# Revit family: 1000_Sliding_Window_XO_Standard
name_source: partatom
category: Windows
revit_build: Autodesk Revit 2014 (Build: 20130308_1515(x64)
units: mm (PartAtom-declared; Revit-internal decimal feet)

## types (120) — shared parameters
Centered In Wall = Yes
Default Sill Height = 800 mm
Description = Sliding window, XO
Equal Sash Width = Yes
Frame Thickness = 76 mm
Limit Sash Height Max = 1800 mm  [stored 5.90551 ft]
Limit Sash Height Min = 300 mm
Limit Sash Width Max = 1500 mm  [stored 4.92126 ft]
Limit Sash Width Min = 300 mm
Limit Window Height Max = 1857 mm
Limit Window Height Min = 357 mm
Limit Window Width Max = 2999 mm
Limit Window Width Min = 599 mm
Manufacturer = Crealco
Model = 1000
Sash Frame Seal = 2 mm  [stored 0.00656168 ft]
URL = http://www.crealco.co.za
Wall Closure = By host
zero-valued in all types: Custom Frame Offset From Exterior, Custom Sash Width Left

## per-type parameters (varying)
- 1000SW-0906XO-1000Pa: Area Left Sash Glazing=0.15 m²; Area Right Sash Glazing=0.15 m²; Clearvue SHGC Value=0.521; Clearvue U Value=6.66; Custom Windload=1000 mm  [stored 3.28084 ft]; Custom Window Height=590 mm  [stored 1.9357 ft]; Custom Window Width=890 mm  [stored 2.91995 ft]; Energy Advantage SHGC Value=0.469; Energy Advantage U Value=5.64; Heavy Duty Interlocker=No; Height=590 mm  [stored 1.9357 ft]; Intruderprufe LowE SHGC Value=0.429; Intruderprufe LowE U Value=5.22; Intruderprufe SHGC Value=0.492; Intruderprufe U Value=6.2; Is Heavy Duty Mullion=0 mm  [stored 0 ft]; Limit Sash Width Left Max=591 mm; Limit Sash Width Left Min=300 mm; Max Pane Area=0.15 m²; Sash Height=533 mm; Sash Width Left=446 mm; Sash Width Right=446 mm; Standard Interlocker=Yes; Width=890 mm  [stored 2.91995 ft]; Windload Design=1000 mm  [stored 3.28084 ft]
- 1000SW-1206XO-1000Pa: Area Left Sash Glazing=0.21 m²; Area Right Sash Glazing=0.21 m²; Clearvue SHGC Value=0.546; Clearvue U Value=6.69; Custom Windload=1000 mm  [stored 3.28084 ft]; Custom Window Height=590 mm  [stored 1.9357 ft]; Custom Window Width=1190 mm  [stored 3.9042 ft]; Energy Advantage SHGC Value=0.491; Energy Advantage U Value=5.56; Heavy Duty Interlocker=No; Height=590 mm  [stored 1.9357 ft]; Intruderprufe LowE SHGC Value=0.449; Intruderprufe LowE U Value=5.14; Intruderprufe SHGC Value=0.515; Intruderprufe U Value=6.22; Is Heavy Duty Mullion=0 mm  [stored 0 ft]; Limit Sash Width Left Max=891 mm; Limit Sash Width Left Min=300 mm; Max Pane Area=0.21 m²; Sash Height=533 mm; Sash Width Left=596 mm; Sash Width Right=596 mm; Standard Interlocker=Yes; Width=1190 mm  [stored 3.9042 ft]; Windload Design=1000 mm  [stored 3.28084 ft]
- 1000SW-1506XO-1000Pa: Area Left Sash Glazing=0.28 m²; Area Right Sash Glazing=0.28 m²; Clearvue SHGC Value=0.562; Clearvue U Value=6.71; Custom Windload=1000 mm  [stored 3.28084 ft]; Custom Window Height=590 mm  [stored 1.9357 ft]; Custom Window Width=1490 mm  [stored 4.88845 ft]; Energy Advantage SHGC Value=0.505; Energy Advantage U Value=5.52; Heavy Duty Interlocker=No; Height=590 mm  [stored 1.9357 ft]; Intruderprufe LowE SHGC Value=0.461; Intruderprufe LowE U Value=5.08; Intruderprufe SHGC Value=0.529; Intruderprufe U Value=6.23; Is Heavy Duty Mullion=0 mm  [stored 0 ft]; Limit Sash Width Left Max=1191 mm; Limit Sash Width Left Min=300 mm; Max Pane Area=0.28 m²; Sash Height=533 mm; Sash Width Left=746 mm; Sash Width Right=746 mm; Standard Interlocker=Yes; Width=1490 mm  [stored 4.88845 ft]; Windload Design=1000 mm  [stored 3.28084 ft]
- 1000SW-1806XO-1000Pa: Area Left Sash Glazing=0.34 m²; Area Right Sash Glazing=0.34 m²; Clearvue SHGC Value=0.572; Clearvue U Value=6.73; Custom Windload=1000 mm  [stored 3.28084 ft]; Custom Window Height=590 mm  [stored 1.9357 ft]; Custom Window Width=1790 mm  [stored 5.8727 ft]; Energy Advantage SHGC Value=0.513; Energy Advantage U Value=5.49; Heavy Duty Interlocker=No; Height=590 mm  [stored 1.9357 ft]; Intruderprufe LowE SHGC Value=4.69; Intruderprufe LowE U Value=5.05; Intruderprufe SHGC Value=0.539; Intruderprufe U Value=6.24; Is Heavy Duty Mullion=0 mm  [stored 0 ft]; Limit Sash Width Left Max=1491 mm; Limit Sash Width Left Min=300 mm; Max Pane Area=0.34 m²; Sash Height=533 mm; Sash Width Left=896 mm; Sash Width Right=896 mm; Standard Interlocker=Yes; Width=1790 mm  [stored 5.8727 ft]; Windload Design=1000 mm  [stored 3.28084 ft]
- 1000SW-2106XO-1000Pa: Area Left Sash Glazing=0.41 m²; Area Right Sash Glazing=0.41 m²; Clearvue SHGC Value=0.579; Clearvue U Value=6.74; Custom Windload=1000 mm  [stored 3.28084 ft]; Custom Window Height=590 mm  [stored 1.9357 ft]; Custom Window Width=2090 mm  [stored 6.85696 ft]; Energy Advantage SHGC Value=0.52; Energy Advantage U Value=5.47; Heavy Duty Interlocker=No; Height=590 mm  [stored 1.9357 ft]; Intruderprufe LowE SHGC Value=0.474; Intruderprufe LowE U Value=5.02; Intruderprufe SHGC Value=0.545; Intruderprufe U Value=6.24; Is Heavy Duty Mullion=0 mm  [stored 0 ft]; Limit Sash Width Left Max=1500 mm  [stored 4.92126 ft]; Limit Sash Width Left Min=591 mm; Max Pane Area=0.41 m²; Sash Height=533 mm; Sash Width Left=1046 mm; Sash Width Right=1046 mm; Standard Interlocker=Yes; Width=2090 mm  [stored 6.85696 ft]; Windload Design=1000 mm  [stored 3.28084 ft]
- 1000SW-2406XO-1000Pa: Area Left Sash Glazing=0.47 m²; Area Right Sash Glazing=0.47 m²; Clearvue SHGC Value=0.584; Clearvue U Value=6.75; Custom Windload=1000 mm  [stored 3.28084 ft]; Custom Window Height=590 mm  [stored 1.9357 ft]; Custom Window Width=2390 mm  [stored 7.84121 ft]; Energy Advantage SHGC Value=0.524; Energy Advantage U Value=5.46; Heavy Duty Interlocker=No; Height=590 mm  [stored 1.9357 ft]; Intruderprufe LowE SHGC Value=0.479; Intruderprufe LowE U Value=5; Intruderprufe SHGC Value=0.55; Intruderprufe U Value=6.25; Is Heavy Duty Mullion=0 mm  [stored 0 ft]; Limit Sash Width Left Max=1500 mm  [stored 4.92126 ft]; Limit Sash Width Left Min=891 mm; Max Pane Area=0.47 m²; Sash Height=533 mm; Sash Width Left=1196 mm; Sash Width Right=1196 mm; Standard Interlocker=Yes; Width=2390 mm  [stored 7.84121 ft]; Windload Design=1000 mm  [stored 3.28084 ft]
- 1000SW-2706XO-1000Pa: Area Left Sash Glazing=0.54 m²; Area Right Sash Glazing=0.54 m²; Clearvue SHGC Value=0.588; Clearvue U Value=6.75; Custom Windload=1000 mm  [stored 3.28084 ft]; Custom Window Height=590 mm  [stored 1.9357 ft]; Custom Window Width=2690 mm; Energy Advantage SHGC Value=0.528; Energy Advantage U Value=5.44; Heavy Duty Interlocker=No; Height=590 mm  [stored 1.9357 ft]; Intruderprufe LowE SHGC Value=0.482; Intruderprufe LowE U Value=4.99; Intruderprufe SHGC Value=0.544; Intruderprufe U Value=6.25; Is Heavy Duty Mullion=0 mm  [stored 0 ft]; Limit Sash Width Left Max=1500 mm  [stored 4.92126 ft]; Limit Sash Width Left Min=1191 mm; Max Pane Area=0.54 m²; Sash Height=533 mm; Sash Width Left=1346 mm; Sash Width Right=1346 mm; Standard Interlocker=Yes; Width=2690 mm; Windload Design=1000 mm  [stored 3.28084 ft]
- 1000SW-3006XO-1000Pa: Area Left Sash Glazing=0.6 m²; Area Right Sash Glazing=0.6 m²; Clearvue SHGC Value=0.592; Clearvue U Value=6.76; Custom Windload=1000 mm  [stored 3.28084 ft]; Custom Window Height=590 mm  [stored 1.9357 ft]; Custom Window Width=2990 mm  [stored 9.80971 ft]; Energy Advantage SHGC Value=0.531; Energy Advantage U Value=5.43; Heavy Duty Interlocker=No; Height=590 mm  [stored 1.9357 ft]; Intruderprufe LowE SHGC Value=0.484; Intruderprufe LowE U Value=4.98; Intruderprufe SHGC Value=0.557; Intruderprufe U Value=6.25; Is Heavy Duty Mullion=0 mm  [stored 0 ft]; Limit Sash Width Left Max=1500 mm  [stored 4.92126 ft]; Limit Sash Width Left Min=1491 mm; Max Pane Area=0.6 m²; Sash Height=533 mm; Sash Width Left=1496 mm; Sash Width Right=1496 mm; Standard Interlocker=Yes; Width=2990 mm  [stored 9.80971 ft]; Windload Design=1000 mm  [stored 3.28084 ft]
- 1000SW-0909XO-1000Pa: Area Left Sash Glazing=0.25 m²; Area Right Sash Glazing=0.25 m²; Clearvue SHGC Value=0.585; Clearvue U Value=6.4; Custom Windload=1000 mm  [stored 3.28084 ft]; Custom Window Height=890 mm  [stored 2.91995 ft]; Custom Window Width=890 mm  [stored 2.91995 ft]; Energy Advantage SHGC Value=0.525; Energy Advantage U Value=5.21; Heavy Duty Interlocker=No; Height=890 mm  [stored 2.91995 ft]; Intruderprufe LowE SHGC Value=0.485; Intruderprufe LowE U Value=4.91; Intruderprufe SHGC Value=0.554; Intruderprufe U Value=6.05; Is Heavy Duty Mullion=0 mm  [stored 0 ft]; Limit Sash Width Left Max=591 mm; Limit Sash Width Left Min=300 mm; Max Pane Area=0.25 m²; Sash Height=833 mm; Sash Width Left=446 mm; Sash Width Right=446 mm; Standard Interlocker=Yes; Width=890 mm  [stored 2.91995 ft]; Windload Design=1000 mm  [stored 3.28084 ft]
- 1000SW-1209XO-1000Pa: Area Left Sash Glazing=0.36 m²; Area Right Sash Glazing=0.36 m²; Clearvue SHGC Value=0.614; Clearvue U Value=6.42; Custom Windload=1000 mm  [stored 3.28084 ft]; Custom Window Height=890 mm  [stored 2.91995 ft]; Custom Window Width=1190 mm  [stored 3.9042 ft]; Energy Advantage SHGC Value=0.55; Energy Advantage U Value=5.11; Heavy Duty Interlocker=No; Height=890 mm  [stored 2.91995 ft]; Intruderprufe LowE SHGC Value=0.507; Intruderprufe LowE U Value=4.8; Intruderprufe SHGC Value=0.58; Intruderprufe U Value=6.06; Is Heavy Duty Mullion=0 mm  [stored 0 ft]; Limit Sash Width Left Max=891 mm; Limit Sash Width Left Min=300 mm; Max Pane Area=0.36 m²; Sash Height=833 mm; Sash Width Left=596 mm; Sash Width Right=596 mm; Standard Interlocker=Yes; Width=1190 mm  [stored 3.9042 ft]; Windload Design=1000 mm  [stored 3.28084 ft]
- 1000SW-1509XO-1000Pa: Area Left Sash Glazing=0.47 m²; Area Right Sash Glazing=0.47 m²; Clearvue SHGC Value=0.631; Clearvue U Value=6.43; Custom Windload=1000 mm  [stored 3.28084 ft]; Custom Window Height=890 mm  [stored 2.91995 ft]; Custom Window Width=1490 mm  [stored 4.88845 ft]; Energy Advantage SHGC Value=0.565; Energy Advantage U Value=5.04; Heavy Duty Interlocker=No; Height=890 mm  [stored 2.91995 ft]; Intruderprufe LowE SHGC Value=0.521; Intruderprufe LowE U Value=4.73; Intruderprufe SHGC Value=0.596; Intruderprufe U Value=6.07; Is Heavy Duty Mullion=0 mm  [stored 0 ft]; Limit Sash Width Left Max=1191 mm; Limit Sash Width Left Min=300 mm; Max Pane Area=0.47 m²; Sash Height=833 mm; Sash Width Left=746 mm; Sash Width Right=746 mm; Standard Interlocker=Yes; Width=1490 mm  [stored 4.88845 ft]; Windload Design=1000 mm  [stored 3.28084 ft]
- 1000SW-1809XO-1000Pa: Area Left Sash Glazing=0.58 m²; Area Right Sash Glazing=0.58 m²; Clearvue SHGC Value=0.642; Clearvue U Value=6.44; Custom Windload=1000 mm  [stored 3.28084 ft]; Custom Window Height=890 mm  [stored 2.91995 ft]; Custom Window Width=1790 mm  [stored 5.8727 ft]; Energy Advantage SHGC Value=0.575; Energy Advantage U Value=5; Heavy Duty Interlocker=No; Height=890 mm  [stored 2.91995 ft]; Intruderprufe LowE SHGC Value=0.53; Intruderprufe LowE U Value=4.68; Intruderprufe SHGC Value=0.607; Intruderprufe U Value=6.08; Is Heavy Duty Mullion=0 mm  [stored 0 ft]; Limit Sash Width Left Max=1491 mm; Limit Sash Width Left Min=300 mm; Max Pane Area=0.58 m²; Sash Height=833 mm; Sash Width Left=896 mm; Sash Width Right=896 mm; Standard Interlocker=Yes; Width=1790 mm  [stored 5.8727 ft]; Windload Design=1000 mm  [stored 3.28084 ft]
- 1000SW-2109XO-1000Pa: Area Left Sash Glazing=0.69 m²; Area Right Sash Glazing=0.69 m²; Clearvue SHGC Value=0.65; Clearvue U Value=6.45; Custom Windload=1000 mm  [stored 3.28084 ft]; Custom Window Height=890 mm  [stored 2.91995 ft]; Custom Window Width=2090 mm  [stored 6.85696 ft]; Energy Advantage SHGC Value=0.583; Energy Advantage U Value=4.97; Heavy Duty Interlocker=No; Height=890 mm  [stored 2.91995 ft]; Intruderprufe LowE SHGC Value=0.536; Intruderprufe LowE U Value=4.65; Intruderprufe SHGC Value=0.614; Intruderprufe U Value=6.08; Is Heavy Duty Mullion=0 mm  [stored 0 ft]; Limit Sash Width Left Max=1500 mm  [stored 4.92126 ft]; Limit Sash Width Left Min=591 mm; Max Pane Area=0.69 m²; Sash Height=833 mm; Sash Width Left=1046 mm; Sash Width Right=1046 mm; Standard Interlocker=Yes; Width=2090 mm  [stored 6.85696 ft]; Windload Design=1000 mm  [stored 3.28084 ft]
- 1000SW-2409XO-1000Pa: Area Left Sash Glazing=0.8 m²; Area Right Sash Glazing=0.8 m²; Clearvue SHGC Value=0.656; Clearvue U Value=6.45; Custom Windload=1000 mm  [stored 3.28084 ft]; Custom Window Height=890 mm  [stored 2.91995 ft]; Custom Window Width=2390 mm  [stored 7.84121 ft]; Energy Advantage SHGC Value=0.588; Energy Advantage U Value=4.95; Heavy Duty Interlocker=No; Height=890 mm  [stored 2.91995 ft]; Intruderprufe LowE SHGC Value=0.541; Intruderprufe LowE U Value=4.62; Intruderprufe SHGC Value=0.62; Intruderprufe U Value=6.08; Is Heavy Duty Mullion=0 mm  [stored 0 ft]; Limit Sash Width Left Max=1500 mm  [stored 4.92126 ft]; Limit Sash Width Left Min=891 mm; Max Pane Area=0.8 m²; Sash Height=833 mm; Sash Width Left=1196 mm; Sash Width Right=1196 mm; Standard Interlocker=Yes; Width=2390 mm  [stored 7.84121 ft]; Windload Design=1000 mm  [stored 3.28084 ft]
- 1000SW-2709XO-1000Pa: Area Left Sash Glazing=0.91 m²; Area Right Sash Glazing=0.91 m²; Clearvue SHGC Value=0.661; Clearvue U Value=6.46; Custom Windload=1000 mm  [stored 3.28084 ft]; Custom Window Height=890 mm  [stored 2.91995 ft]; Custom Window Width=2690 mm; Energy Advantage SHGC Value=0.592; Energy Advantage U Value=4.93; Heavy Duty Interlocker=No; Height=890 mm  [stored 2.91995 ft]; Intruderprufe LowE SHGC Value=0.545; Intruderprufe LowE U Value=4.61; Intruderprufe SHGC Value=0.624; Intruderprufe U Value=6.08; Is Heavy Duty Mullion=0 mm  [stored 0 ft]; Limit Sash Width Left Max=1500 mm  [stored 4.92126 ft]; Limit Sash Width Left Min=1191 mm; Max Pane Area=0.91 m²; Sash Height=833 mm; Sash Width Left=1346 mm; Sash Width Right=1346 mm; Standard Interlocker=Yes; Width=2690 mm; Windload Design=1000 mm  [stored 3.28084 ft]
- 1000SW-3009XO-1000Pa: Area Left Sash Glazing=1.02 m²; Area Right Sash Glazing=1.02 m²; Clearvue SHGC Value=0.665; Clearvue U Value=6.46; Custom Windload=1000 mm  [stored 3.28084 ft]; Custom Window Height=890 mm  [stored 2.91995 ft]; Custom Window Width=2990 mm  [stored 9.80971 ft]; Energy Advantage SHGC Value=0.595; Energy Advantage U Value=4.92; Heavy Duty Interlocker=No; Height=890 mm  [stored 2.91995 ft]; Intruderprufe LowE SHGC Value=0.548; Intruderprufe LowE U Value=4.59; Intruderprufe SHGC Value=0.628; Intruderprufe U Value=6.08; Is Heavy Duty Mullion=0 mm  [stored 0 ft]; Limit Sash Width Left Max=1500 mm  [stored 4.92126 ft]; Limit Sash Width Left Min=1491 mm; Max Pane Area=1.02 m²; Sash Height=833 mm; Sash Width Left=1496 mm; Sash Width Right=1496 mm; Standard Interlocker=Yes; Width=2990 mm  [stored 9.80971 ft]; Windload Design=1000 mm  [stored 3.28084 ft]
- 1000SW-0912XO-1000Pa: Area Left Sash Glazing=0.36 m²; Area Right Sash Glazing=0.36 m²; Clearvue SHGC Value=0.616; Clearvue U Value=6.27; Custom Windload=1000 mm  [stored 3.28084 ft]; Custom Window Height=1190 mm  [stored 3.9042 ft]; Custom Window Width=890 mm  [stored 2.91995 ft]; Energy Advantage SHGC Value=0.553; Energy Advantage U Value=5; Heavy Duty Interlocker=No; Height=1190 mm  [stored 3.9042 ft]; Intruderprufe LowE SHGC Value=0.512; Intruderprufe LowE U Value=4.76; Intruderprufe SHGC Value=0.584; Intruderprufe U Value=5.98; Is Heavy Duty Mullion=0 mm  [stored 0 ft]; Limit Sash Width Left Max=591 mm; Limit Sash Width Left Min=300 mm; Max Pane Area=0.36 m²; Sash Height=1133 mm; Sash Width Left=446 mm; Sash Width Right=446 mm; Standard Interlocker=Yes; Width=890 mm  [stored 2.91995 ft]; Windload Design=1000 mm  [stored 3.28084 ft]
- 1000SW-1212XO-1000Pa: Area Left Sash Glazing=0.51 m²; Area Right Sash Glazing=0.51 m²; Clearvue SHGC Value=0.647; Clearvue U Value=6.29; Custom Windload=1000 mm  [stored 3.28084 ft]; Custom Window Height=1190 mm  [stored 3.9042 ft]; Custom Window Width=1190 mm  [stored 3.9042 ft]; Energy Advantage SHGC Value=0.58; Energy Advantage U Value=4.88; Heavy Duty Interlocker=No; Height=1190 mm  [stored 3.9042 ft]; Intruderprufe LowE SHGC Value=0.536; Intruderprufe LowE U Value=4.63; Intruderprufe SHGC Value=0.613; Intruderprufe U Value=5.99; Is Heavy Duty Mullion=0 mm  [stored 0 ft]; Limit Sash Width Left Max=891 mm; Limit Sash Width Left Min=300 mm; Max Pane Area=0.51 m²; Sash Height=1133 mm; Sash Width Left=596 mm; Sash Width Right=596 mm; Standard Interlocker=Yes; Width=1190 mm  [stored 3.9042 ft]; Windload Design=1000 mm  [stored 3.28084 ft]
- 1000SW-1512XO-1000Pa: Area Left Sash Glazing=0.67 m²; Area Right Sash Glazing=0.67 m²; Clearvue SHGC Value=0.665; Clearvue U Value=6.3; Custom Windload=1000 mm  [stored 3.28084 ft]; Custom Window Height=1190 mm  [stored 3.9042 ft]; Custom Window Width=1490 mm  [stored 4.88845 ft]; Energy Advantage SHGC Value=0.596; Energy Advantage U Value=4.81; Heavy Duty Interlocker=No; Height=1190 mm  [stored 3.9042 ft]; Intruderprufe LowE SHGC Value=0.55; Intruderprufe LowE U Value=4; Intruderprufe SHGC Value=0.629; Intruderprufe U Value=5.99; Is Heavy Duty Mullion=0 mm  [stored 0 ft]; Limit Sash Width Left Max=1191 mm; Limit Sash Width Left Min=300 mm; Max Pane Area=0.67 m²; Sash Height=1133 mm; Sash Width Left=746 mm; Sash Width Right=746 mm; Standard Interlocker=Yes; Width=1490 mm  [stored 4.88845 ft]; Windload Design=1000 mm  [stored 3.28084 ft]
- 1000SW-1812XO-1000Pa: Area Left Sash Glazing=0.82 m²; Area Right Sash Glazing=0.82 m²; Clearvue SHGC Value=0.677; Clearvue U Value=6.3; Custom Windload=1000 mm  [stored 3.28084 ft]; Custom Window Height=1190 mm  [stored 3.9042 ft]; Custom Window Width=1790 mm  [stored 5.8727 ft]; Energy Advantage SHGC Value=0.606; Energy Advantage U Value=4.76; Heavy Duty Interlocker=No; Height=1190 mm  [stored 3.9042 ft]; Intruderprufe LowE SHGC Value=0.56; Intruderprufe LowE U Value=4.5; Intruderprufe SHGC Value=0.641; Intruderprufe U Value=5.99; Is Heavy Duty Mullion=0 mm  [stored 0 ft]; Limit Sash Width Left Max=1491 mm; Limit Sash Width Left Min=300 mm; Max Pane Area=0.82 m²; Sash Height=1133 mm; Sash Width Left=896 mm; Sash Width Right=896 mm; Standard Interlocker=Yes; Width=1790 mm  [stored 5.8727 ft]; Windload Design=1000 mm  [stored 3.28084 ft]
- 1000SW-2112XO-1000Pa: Area Left Sash Glazing=0.98 m²; Area Right Sash Glazing=0.98 m²; Clearvue SHGC Value=0.686; Clearvue U Value=6.31; Custom Windload=1000 mm  [stored 3.28084 ft]; Custom Window Height=1190 mm  [stored 3.9042 ft]; Custom Window Width=2090 mm  [stored 6.85696 ft]; Energy Advantage SHGC Value=0.614; Energy Advantage U Value=4.72; Heavy Duty Interlocker=No; Height=1190 mm  [stored 3.9042 ft]; Intruderprufe LowE SHGC Value=0.567; Intruderprufe LowE U Value=4.46; Intruderprufe SHGC Value=0.649; Intruderprufe U Value=6; Is Heavy Duty Mullion=0 mm  [stored 0 ft]; Limit Sash Width Left Max=1500 mm  [stored 4.92126 ft]; Limit Sash Width Left Min=591 mm; Max Pane Area=0.98 m²; Sash Height=1133 mm; Sash Width Left=1046 mm; Sash Width Right=1046 mm; Standard Interlocker=Yes; Width=2090 mm  [stored 6.85696 ft]; Windload Design=1000 mm  [stored 3.28084 ft]
- 1000SW-2412XO-1000Pa: Area Left Sash Glazing=1.13 m²; Area Right Sash Glazing=1.13 m²; Clearvue SHGC Value=0.692; Clearvue U Value=6.31; Custom Windload=1000 mm  [stored 3.28084 ft]; Custom Window Height=1190 mm  [stored 3.9042 ft]; Custom Window Width=2390 mm  [stored 7.84121 ft]; Energy Advantage SHGC Value=0.619; Energy Advantage U Value=4.7; Heavy Duty Interlocker=No; Height=1190 mm  [stored 3.9042 ft]; Intruderprufe LowE SHGC Value=0.572; Intruderprufe LowE U Value=4.44; Intruderprufe SHGC Value=0.655; Intruderprufe U Value=6; Is Heavy Duty Mullion=0 mm  [stored 0 ft]; Limit Sash Width Left Max=1500 mm  [stored 4.92126 ft]; Limit Sash Width Left Min=891 mm; Max Pane Area=1.13 m²; Sash Height=1133 mm; Sash Width Left=1196 mm; Sash Width Right=1196 mm; Standard Interlocker=Yes; Width=2390 mm  [stored 7.84121 ft]; Windload Design=1000 mm  [stored 3.28084 ft]
- 1000SW-2712XO-1000Pa: Area Left Sash Glazing=1.28 m²; Area Right Sash Glazing=1.28 m²; Clearvue SHGC Value=0.679; Clearvue U Value=6.31; Custom Windload=1000 mm  [stored 3.28084 ft]; Custom Window Height=1190 mm  [stored 3.9042 ft]; Custom Window Width=2690 mm; Energy Advantage SHGC Value=0.624; Energy Advantage U Value=4.68; Heavy Duty Interlocker=No; Height=1190 mm  [stored 3.9042 ft]; Intruderprufe LowE SHGC Value=0.576; Intruderprufe LowE U Value=4.42; Intruderprufe SHGC Value=0.659; Intruderprufe U Value=6; Is Heavy Duty Mullion=0 mm  [stored 0 ft]; Limit Sash Width Left Max=1500 mm  [stored 4.92126 ft]; Limit Sash Width Left Min=1191 mm; Max Pane Area=1.28 m²; Sash Height=1133 mm; Sash Width Left=1346 mm; Sash Width Right=1346 mm; Standard Interlocker=Yes; Width=2690 mm; Windload Design=1000 mm  [stored 3.28084 ft]
- 1000SW-3012XO-1000Pa: Area Left Sash Glazing=1.44 m²; Area Right Sash Glazing=1.44 m²; Clearvue SHGC Value=0.701; Clearvue U Value=6.31; Custom Windload=1000 mm  [stored 3.28084 ft]; Custom Window Height=1190 mm  [stored 3.9042 ft]; Custom Window Width=2990 mm  [stored 9.80971 ft]; Energy Advantage SHGC Value=0.627; Energy Advantage U Value=4.66; Heavy Duty Interlocker=No; Height=1190 mm  [stored 3.9042 ft]; Intruderprufe LowE SHGC Value=0.579; Intruderprufe LowE U Value=4.4; Intruderprufe SHGC Value=0.663; Intruderprufe U Value=6; Is Heavy Duty Mullion=0 mm  [stored 0 ft]; Limit Sash Width Left Max=1500 mm  [stored 4.92126 ft]; Limit Sash Width Left Min=1491 mm; Max Pane Area=1.44 m²; Sash Height=1133 mm; Sash Width Left=1496 mm; Sash Width Right=1496 mm; Standard Interlocker=Yes; Width=2990 mm  [stored 9.80971 ft]; Windload Design=1000 mm  [stored 3.28084 ft]
- 1000SW-0915XO-1000Pa: Area Left Sash Glazing=0.46 m²; Area Right Sash Glazing=0.46 m²; Clearvue SHGC Value=0.635; Clearvue U Value=6.19; Custom Windload=1000 mm  [stored 3.28084 ft]; Custom Window Height=1490 mm  [stored 4.88845 ft]; Custom Window Width=890 mm  [stored 2.91995 ft]; Energy Advantage SHGC Value=0.57; Energy Advantage U Value=4.87; Heavy Duty Interlocker=No; Height=1490 mm  [stored 4.88845 ft]; Intruderprufe LowE SHGC Value=0.528; Intruderprufe LowE U Value=4.67; Intruderprufe SHGC Value=0.603; Intruderprufe U Value=5.94; Is Heavy Duty Mullion=0 mm  [stored 0 ft]; Limit Sash Width Left Max=591 mm; Limit Sash Width Left Min=300 mm; Max Pane Area=0.46 m²; Sash Height=1433 mm; Sash Width Left=446 mm; Sash Width Right=446 mm; Standard Interlocker=Yes; Width=890 mm  [stored 2.91995 ft]; Windload Design=1000 mm  [stored 3.28084 ft]
- 1000SW-1215XO-1000Pa: Area Left Sash Glazing=0.66 m²; Area Right Sash Glazing=0.66 m²; Clearvue SHGC Value=0.667; Clearvue U Value=6.2; Custom Windload=1000 mm  [stored 3.28084 ft]; Custom Window Height=1490 mm  [stored 4.88845 ft]; Custom Window Width=1190 mm  [stored 3.9042 ft]; Energy Advantage SHGC Value=0.597; Energy Advantage U Value=4.74; Heavy Duty Interlocker=No; Height=1490 mm  [stored 4.88845 ft]; Intruderprufe LowE SHGC Value=0.553; Intruderprufe LowE U Value=4.53; Intruderprufe SHGC Value=0.632; Intruderprufe U Value=5.94; Is Heavy Duty Mullion=0 mm  [stored 0 ft]; Limit Sash Width Left Max=891 mm; Limit Sash Width Left Min=300 mm; Max Pane Area=0.66 m²; Sash Height=1433 mm; Sash Width Left=596 mm; Sash Width Right=596 mm; Standard Interlocker=Yes; Width=1190 mm  [stored 3.9042 ft]; Windload Design=1000 mm  [stored 3.28084 ft]
- 1000SW-1515XO-1000Pa: Area Left Sash Glazing=0.86 m²; Area Right Sash Glazing=0.86 m²; Clearvue SHGC Value=0.685; Clearvue U Value=6.21; Custom Windload=1000 mm  [stored 3.28084 ft]; Custom Window Height=1490 mm  [stored 4.88845 ft]; Custom Window Width=1490 mm  [stored 4.88845 ft]; Energy Advantage SHGC Value=0.614; Energy Advantage U Value=4.66; Heavy Duty Interlocker=No; Height=1490 mm  [stored 4.88845 ft]; Intruderprufe LowE SHGC Value=0.568; Intruderprufe LowE U Value=4.45; Intruderprufe SHGC Value=0.649; Intruderprufe U Value=5.94; Is Heavy Duty Mullion=0 mm  [stored 0 ft]; Limit Sash Width Left Max=1191 mm; Limit Sash Width Left Min=300 mm; Max Pane Area=0.86 m²; Sash Height=1433 mm; Sash Width Left=746 mm; Sash Width Right=746 mm; Standard Interlocker=Yes; Width=1490 mm  [stored 4.88845 ft]; Windload Design=1000 mm  [stored 3.28084 ft]
- 1000SW-1815XO-1000Pa: Area Left Sash Glazing=1.06 m²; Area Right Sash Glazing=1.06 m²; Clearvue SHGC Value=0.693; Clearvue U Value=6.22; Custom Windload=1000 mm  [stored 3.28084 ft]; Custom Window Height=1490 mm  [stored 4.88845 ft]; Custom Window Width=1790 mm  [stored 5.8727 ft]; Energy Advantage SHGC Value=0.625; Energy Advantage U Value=4.61; Heavy Duty Interlocker=No; Height=1490 mm  [stored 4.88845 ft]; Intruderprufe LowE SHGC Value=0.578; Intruderprufe LowE U Value=4.39; Intruderprufe SHGC Value=0.661; Intruderprufe U Value=5.95; Is Heavy Duty Mullion=0 mm  [stored 0 ft]; Limit Sash Width Left Max=1491 mm; Limit Sash Width Left Min=300 mm; Max Pane Area=1.06 m²; Sash Height=1433 mm; Sash Width Left=896 mm; Sash Width Right=896 mm; Standard Interlocker=Yes; Width=1790 mm  [stored 5.8727 ft]; Windload Design=1000 mm  [stored 3.28084 ft]
- 1000SW-2115XO-1000Pa: Area Left Sash Glazing=1.26 m²; Area Right Sash Glazing=1.26 m²; Clearvue SHGC Value=0.707; Clearvue U Value=6.22; Custom Windload=1000 mm  [stored 3.28084 ft]; Custom Window Height=1490 mm  [stored 4.88845 ft]; Custom Window Width=2090 mm  [stored 6.85696 ft]; Energy Advantage SHGC Value=0.632; Energy Advantage U Value=6.32; Heavy Duty Interlocker=No; Height=1490 mm  [stored 4.88845 ft]; Intruderprufe LowE SHGC Value=0.585; Intruderprufe LowE U Value=4.35; Intruderprufe SHGC Value=0.669; Intruderprufe U Value=5.95; Is Heavy Duty Mullion=0 mm  [stored 0 ft]; Limit Sash Width Left Max=1500 mm  [stored 4.92126 ft]; Limit Sash Width Left Min=591 mm; Max Pane Area=1.26 m²; Sash Height=1433 mm; Sash Width Left=1046 mm; Sash Width Right=1046 mm; Standard Interlocker=Yes; Width=2090 mm  [stored 6.85696 ft]; Windload Design=1000 mm  [stored 3.28084 ft]
- 1000SW-2415XO-1000Pa: Area Left Sash Glazing=1.46 m²; Area Right Sash Glazing=1.46 m²; Clearvue SHGC Value=0.713; Clearvue U Value=6.22; Custom Windload=1000 mm  [stored 3.28084 ft]; Custom Window Height=1490 mm  [stored 4.88845 ft]; Custom Window Width=2390 mm  [stored 7.84121 ft]; Energy Advantage SHGC Value=0.638; Energy Advantage U Value=4.55; Heavy Duty Interlocker=No; Height=1490 mm  [stored 4.88845 ft]; Intruderprufe LowE SHGC Value=0.59; Intruderprufe LowE U Value=4.33; Intruderprufe SHGC Value=0.675; Intruderprufe U Value=5.95; Is Heavy Duty Mullion=0 mm  [stored 0 ft]; Limit Sash Width Left Max=1500 mm  [stored 4.92126 ft]; Limit Sash Width Left Min=891 mm; Max Pane Area=1.46 m²; Sash Height=1433 mm; Sash Width Left=1196 mm; Sash Width Right=1196 mm; Standard Interlocker=Yes; Width=2390 mm  [stored 7.84121 ft]; Windload Design=1000 mm  [stored 3.28084 ft]
- 1000SW-2715XO-1000Pa: Area Left Sash Glazing=1.66 m²; Area Right Sash Glazing=1.66 m²; Clearvue SHGC Value=0.719; Clearvue U Value=6.23; Custom Windload=1000 mm  [stored 3.28084 ft]; Custom Window Height=1490 mm  [stored 4.88845 ft]; Custom Window Width=2690 mm; Energy Advantage SHGC Value=0.643; Energy Advantage U Value=4.53; Heavy Duty Interlocker=No; Height=1490 mm  [stored 4.88845 ft]; Intruderprufe LowE SHGC Value=0.594; Intruderprufe LowE U Value=4.3; Intruderprufe SHGC Value=0.68; Intruderprufe U Value=5.95; Is Heavy Duty Mullion=0 mm  [stored 0 ft]; Limit Sash Width Left Max=1500 mm  [stored 4.92126 ft]; Limit Sash Width Left Min=1191 mm; Max Pane Area=1.66 m²; Sash Height=1433 mm; Sash Width Left=1346 mm; Sash Width Right=1346 mm; Standard Interlocker=Yes; Width=2690 mm; Windload Design=1000 mm  [stored 3.28084 ft]
- 1000SW-3015XO-1000Pa: Area Left Sash Glazing=1.86 m²; Area Right Sash Glazing=1.86 m²; Clearvue SHGC Value=0.723; Clearvue U Value=6.23; Custom Windload=1000 mm  [stored 3.28084 ft]; Custom Window Height=1490 mm  [stored 4.88845 ft]; Custom Window Width=2990 mm  [stored 9.80971 ft]; Energy Advantage SHGC Value=0.646; Energy Advantage U Value=4.51; Heavy Duty Interlocker=No; Height=1490 mm  [stored 4.88845 ft]; Intruderprufe LowE SHGC Value=0.598; Intruderprufe LowE U Value=4.28; Intruderprufe SHGC Value=0.684; Intruderprufe U Value=5.95; Is Heavy Duty Mullion=0 mm  [stored 0 ft]; Limit Sash Width Left Max=1500 mm  [stored 4.92126 ft]; Limit Sash Width Left Min=1491 mm; Max Pane Area=1.86 m²; Sash Height=1433 mm; Sash Width Left=1496 mm; Sash Width Right=1496 mm; Standard Interlocker=Yes; Width=2990 mm  [stored 9.80971 ft]; Windload Design=1000 mm  [stored 3.28084 ft]
- 1000SW-1518XO-1000Pa: Area Left Sash Glazing=1.05 m²; Area Right Sash Glazing=1.05 m²; Clearvue SHGC Value=0.699; Clearvue U Value=6.16; Custom Windload=1000 mm  [stored 3.28084 ft]; Custom Window Height=1790 mm  [stored 5.8727 ft]; Custom Window Width=1490 mm  [stored 4.88845 ft]; Energy Advantage SHGC Value=0.626; Energy Advantage U Value=4.57; Heavy Duty Interlocker=Yes; Height=1790 mm  [stored 5.8727 ft]; Intruderprufe LowE SHGC Value=0.58; Intruderprufe LowE U Value=4.38; Intruderprufe SHGC Value=0.662; Intruderprufe U Value=5.91; Is Heavy Duty Mullion=1 mm  [stored 0.00328084 ft]; Limit Sash Width Left Max=1191 mm; Limit Sash Width Left Min=300 mm; Max Pane Area=1.05 m²; Sash Height=1733 mm; Sash Width Left=746 mm; Sash Width Right=746 mm; Standard Interlocker=No; Width=1490 mm  [stored 4.88845 ft]; Windload Design=1000 mm  [stored 3.28084 ft]
- 1000SW-1818XO-1000Pa: Area Left Sash Glazing=1.3 m²; Area Right Sash Glazing=1.3 m²; Clearvue SHGC Value=0.712; Clearvue U Value=6.16; Custom Windload=1000 mm  [stored 3.28084 ft]; Custom Window Height=1790 mm  [stored 5.8727 ft]; Custom Window Width=1790 mm  [stored 5.8727 ft]; Energy Advantage SHGC Value=0.637; Energy Advantage U Value=4.52; Heavy Duty Interlocker=Yes; Height=1790 mm  [stored 5.8727 ft]; Intruderprufe LowE SHGC Value=0.59; Intruderprufe LowE U Value=4.32; Intruderprufe SHGC Value=0.674; Intruderprufe U Value=5.91; Is Heavy Duty Mullion=1 mm  [stored 0.00328084 ft]; Limit Sash Width Left Max=1491 mm; Limit Sash Width Left Min=300 mm; Max Pane Area=1.3 m²; Sash Height=1733 mm; Sash Width Left=896 mm; Sash Width Right=896 mm; Standard Interlocker=No; Width=1790 mm  [stored 5.8727 ft]; Windload Design=1000 mm  [stored 3.28084 ft]
- 1000SW-2118XO-1000Pa: Area Left Sash Glazing=1.54 m²; Area Right Sash Glazing=1.54 m²; Clearvue SHGC Value=0.721; Clearvue U Value=6.16; Custom Windload=1000 mm  [stored 3.28084 ft]; Custom Window Height=1790 mm  [stored 5.8727 ft]; Custom Window Width=2090 mm  [stored 6.85696 ft]; Energy Advantage SHGC Value=0.645; Energy Advantage U Value=4.48; Heavy Duty Interlocker=Yes; Height=1790 mm  [stored 5.8727 ft]; Intruderprufe LowE SHGC Value=0.597; Intruderprufe LowE U Value=4.28; Intruderprufe SHGC Value=0.683; Intruderprufe U Value=5.92; Is Heavy Duty Mullion=1 mm  [stored 0.00328084 ft]; Limit Sash Width Left Max=1500 mm  [stored 4.92126 ft]; Limit Sash Width Left Min=591 mm; Max Pane Area=1.54 m²; Sash Height=1733 mm; Sash Width Left=1046 mm; Sash Width Right=1046 mm; Standard Interlocker=No; Width=2090 mm  [stored 6.85696 ft]; Windload Design=1000 mm  [stored 3.28084 ft]
- 1000SW-2418XO-1000Pa: Area Left Sash Glazing=1.79 m²; Area Right Sash Glazing=1.79 m²; Clearvue SHGC Value=0.728; Clearvue U Value=6.17; Custom Windload=1000 mm  [stored 3.28084 ft]; Custom Window Height=1790 mm  [stored 5.8727 ft]; Custom Window Width=2390 mm  [stored 7.84121 ft]; Energy Advantage SHGC Value=0.651; Energy Advantage U Value=4.45; Heavy Duty Interlocker=Yes; Height=1790 mm  [stored 5.8727 ft]; Intruderprufe LowE SHGC Value=0.425; Intruderprufe LowE U Value=4.28; Intruderprufe SHGC Value=0.689; Intruderprufe U Value=5.95; Is Heavy Duty Mullion=1 mm  [stored 0.00328084 ft]; Limit Sash Width Left Max=1500 mm  [stored 4.92126 ft]; Limit Sash Width Left Min=891 mm; Max Pane Area=1.79 m²; Sash Height=1733 mm; Sash Width Left=1196 mm; Sash Width Right=1196 mm; Standard Interlocker=No; Width=2390 mm  [stored 7.84121 ft]; Windload Design=1000 mm  [stored 3.28084 ft]
- 1000SW-2718XO-1000Pa: Area Left Sash Glazing=2.03 m²; Area Right Sash Glazing=2.03 m²; Clearvue SHGC Value=0.733; Clearvue U Value=6.17; Custom Windload=1000 mm  [stored 3.28084 ft]; Custom Window Height=1790 mm  [stored 5.8727 ft]; Custom Window Width=2690 mm; Energy Advantage SHGC Value=0.655; Energy Advantage U Value=4.43; Heavy Duty Interlocker=Yes; Height=1790 mm  [stored 5.8727 ft]; Intruderprufe LowE SHGC Value=0.607; Intruderprufe LowE U Value=4.23; Intruderprufe SHGC Value=0.694; Intruderprufe U Value=5.92; Is Heavy Duty Mullion=1 mm  [stored 0.00328084 ft]; Limit Sash Width Left Max=1500 mm  [stored 4.92126 ft]; Limit Sash Width Left Min=1191 mm; Max Pane Area=2.03 m²; Sash Height=1733 mm; Sash Width Left=1346 mm; Sash Width Right=1346 mm; Standard Interlocker=No; Width=2690 mm; Windload Design=1000 mm  [stored 3.28084 ft]
- 1000SW-3018XO-1000Pa: Area Left Sash Glazing=2.28 m²; Area Right Sash Glazing=2.28 m²; Clearvue SHGC Value=0.737; Clearvue U Value=6.17; Custom Windload=1000 mm  [stored 3.28084 ft]; Custom Window Height=1790 mm  [stored 5.8727 ft]; Custom Window Width=2990 mm  [stored 9.80971 ft]; Energy Advantage SHGC Value=0.659; Energy Advantage U Value=4.41; Heavy Duty Interlocker=Yes; Height=1790 mm  [stored 5.8727 ft]; Intruderprufe LowE SHGC Value=0.61; Intruderprufe LowE U Value=4.21; Intruderprufe SHGC Value=0.698; Intruderprufe U Value=5.92; Is Heavy Duty Mullion=1 mm  [stored 0.00328084 ft]; Limit Sash Width Left Max=1500 mm  [stored 4.92126 ft]; Limit Sash Width Left Min=1491 mm; Max Pane Area=2.28 m²; Sash Height=1733 mm; Sash Width Left=1496 mm; Sash Width Right=1496 mm; Standard Interlocker=No; Width=2990 mm  [stored 9.80971 ft]; Windload Design=1000 mm  [stored 3.28084 ft]
- 1000SW-0918XO-1000Pa: Area Left Sash Glazing=0.56 m²; Area Right Sash Glazing=0.56 m²; Clearvue SHGC Value=0.648; Clearvue U Value=6.14; Custom Windload=1000 mm  [stored 3.28084 ft]; Custom Window Height=1790 mm  [stored 5.8727 ft]; Custom Window Width=890 mm  [stored 2.91995 ft]; Energy Advantage SHGC Value=0.581; Energy Advantage U Value=4.79; Heavy Duty Interlocker=No; Height=1790 mm  [stored 5.8727 ft]; Intruderprufe LowE SHGC Value=0.539; Intruderprufe LowE U Value=4.61; Intruderprufe SHGC Value=0.615; Intruderprufe U Value=5.91; Is Heavy Duty Mullion=0 mm  [stored 0 ft]; Limit Sash Width Left Max=591 mm; Limit Sash Width Left Min=300 mm; Max Pane Area=0.56 m²; Sash Height=1733 mm; Sash Width Left=446 mm; Sash Width Right=446 mm; Standard Interlocker=Yes; Width=890 mm  [stored 2.91995 ft]; Windload Design=1000 mm  [stored 3.28084 ft]
- 1000SW-1218XO-1000Pa: Area Left Sash Glazing=0.81 m²; Area Right Sash Glazing=0.81 m²; Clearvue SHGC Value=0.68; Clearvue U Value=6.15; Custom Windload=1000 mm  [stored 3.28084 ft]; Custom Window Height=1790 mm  [stored 5.8727 ft]; Custom Window Width=1190 mm  [stored 3.9042 ft]; Energy Advantage SHGC Value=0.609; Energy Advantage U Value=4.65; Heavy Duty Interlocker=No; Height=1790 mm  [stored 5.8727 ft]; Intruderprufe LowE SHGC Value=0.565; Intruderprufe LowE U Value=4.46; Intruderprufe SHGC Value=0.645; Intruderprufe U Value=5.91; Is Heavy Duty Mullion=0 mm  [stored 0 ft]; Limit Sash Width Left Max=891 mm; Limit Sash Width Left Min=300 mm; Max Pane Area=0.81 m²; Sash Height=1733 mm; Sash Width Left=596 mm; Sash Width Right=596 mm; Standard Interlocker=Yes; Width=1190 mm  [stored 3.9042 ft]; Windload Design=1000 mm  [stored 3.28084 ft]
- 1000SW-0906XO-1500Pa: Area Left Sash Glazing=0.15 m²; Area Right Sash Glazing=0.15 m²; Clearvue SHGC Value=0.521; Clearvue U Value=6.66; Custom Windload=1500 mm  [stored 4.92126 ft]; Custom Window Height=590 mm  [stored 1.9357 ft]; Custom Window Width=890 mm  [stored 2.91995 ft]; Energy Advantage SHGC Value=0.469; Energy Advantage U Value=5.64; Heavy Duty Interlocker=No; Height=590 mm  [stored 1.9357 ft]; Intruderprufe LowE SHGC Value=0.429; Intruderprufe LowE U Value=5.22; Intruderprufe SHGC Value=0.492; Intruderprufe U Value=6.2; Is Heavy Duty Mullion=0 mm  [stored 0 ft]; Limit Sash Width Left Max=591 mm; Limit Sash Width Left Min=300 mm; Max Pane Area=0.15 m²; Sash Height=533 mm; Sash Width Left=446 mm; Sash Width Right=446 mm; Standard Interlocker=Yes; Width=890 mm  [stored 2.91995 ft]; Windload Design=1500 mm  [stored 4.92126 ft]
- 1000SW-0906XO-2000Pa: Area Left Sash Glazing=0.15 m²; Area Right Sash Glazing=0.15 m²; Clearvue SHGC Value=0.521; Clearvue U Value=6.66; Custom Windload=2000 mm  [stored 6.56168 ft]; Custom Window Height=590 mm  [stored 1.9357 ft]; Custom Window Width=890 mm  [stored 2.91995 ft]; Energy Advantage SHGC Value=0.469; Energy Advantage U Value=5.64; Heavy Duty Interlocker=No; Height=590 mm  [stored 1.9357 ft]; Intruderprufe LowE SHGC Value=0.429; Intruderprufe LowE U Value=5.22; Intruderprufe SHGC Value=0.492; Intruderprufe U Value=6.2; Is Heavy Duty Mullion=0 mm  [stored 0 ft]; Limit Sash Width Left Max=591 mm; Limit Sash Width Left Min=300 mm; Max Pane Area=0.15 m²; Sash Height=533 mm; Sash Width Left=446 mm; Sash Width Right=446 mm; Standard Interlocker=Yes; Width=890 mm  [stored 2.91995 ft]; Windload Design=2000 mm  [stored 6.56168 ft]
- 1000SW-0909XO-1500Pa: Area Left Sash Glazing=0.25 m²; Area Right Sash Glazing=0.25 m²; Clearvue SHGC Value=0.585; Clearvue U Value=6.4; Custom Windload=1500 mm  [stored 4.92126 ft]; Custom Window Height=890 mm  [stored 2.91995 ft]; Custom Window Width=890 mm  [stored 2.91995 ft]; Energy Advantage SHGC Value=0.525; Energy Advantage U Value=5.21; Heavy Duty Interlocker=No; Height=890 mm  [stored 2.91995 ft]; Intruderprufe LowE SHGC Value=0.485; Intruderprufe LowE U Value=4.91; Intruderprufe SHGC Value=0.554; Intruderprufe U Value=6.05; Is Heavy Duty Mullion=0 mm  [stored 0 ft]; Limit Sash Width Left Max=591 mm; Limit Sash Width Left Min=300 mm; Max Pane Area=0.25 m²; Sash Height=833 mm; Sash Width Left=446 mm; Sash Width Right=446 mm; Standard Interlocker=Yes; Width=890 mm  [stored 2.91995 ft]; Windload Design=1500 mm  [stored 4.92126 ft]
- 1000SW-0909XO-2000Pa: Area Left Sash Glazing=0.25 m²; Area Right Sash Glazing=0.25 m²; Clearvue SHGC Value=0.585; Clearvue U Value=6.4; Custom Windload=2000 mm  [stored 6.56168 ft]; Custom Window Height=890 mm  [stored 2.91995 ft]; Custom Window Width=890 mm  [stored 2.91995 ft]; Energy Advantage SHGC Value=0.525; Energy Advantage U Value=5.21; Heavy Duty Interlocker=No; Height=890 mm  [stored 2.91995 ft]; Intruderprufe LowE SHGC Value=0.485; Intruderprufe LowE U Value=4.91; Intruderprufe SHGC Value=0.554; Intruderprufe U Value=6.05; Is Heavy Duty Mullion=0 mm  [stored 0 ft]; Limit Sash Width Left Max=591 mm; Limit Sash Width Left Min=300 mm; Max Pane Area=0.25 m²; Sash Height=833 mm; Sash Width Left=446 mm; Sash Width Right=446 mm; Standard Interlocker=Yes; Width=890 mm  [stored 2.91995 ft]; Windload Design=2000 mm  [stored 6.56168 ft]
- 1000SW-0912XO-1500Pa: Area Left Sash Glazing=0.36 m²; Area Right Sash Glazing=0.36 m²; Clearvue SHGC Value=0.616; Clearvue U Value=6.27; Custom Windload=1500 mm  [stored 4.92126 ft]; Custom Window Height=1190 mm  [stored 3.9042 ft]; Custom Window Width=890 mm  [stored 2.91995 ft]; Energy Advantage SHGC Value=0.553; Energy Advantage U Value=5; Heavy Duty Interlocker=No; Height=1190 mm  [stored 3.9042 ft]; Intruderprufe LowE SHGC Value=0.512; Intruderprufe LowE U Value=4.76; Intruderprufe SHGC Value=0.584; Intruderprufe U Value=5.98; Is Heavy Duty Mullion=0 mm  [stored 0 ft]; Limit Sash Width Left Max=591 mm; Limit Sash Width Left Min=300 mm; Max Pane Area=0.36 m²; Sash Height=1133 mm; Sash Width Left=446 mm; Sash Width Right=446 mm; Standard Interlocker=Yes; Width=890 mm  [stored 2.91995 ft]; Windload Design=1500 mm  [stored 4.92126 ft]
- 1000SW-0912XO-2000Pa: Area Left Sash Glazing=0.36 m²; Area Right Sash Glazing=0.36 m²; Clearvue SHGC Value=0.616; Clearvue U Value=6.27; Custom Windload=2000 mm  [stored 6.56168 ft]; Custom Window Height=1190 mm  [stored 3.9042 ft]; Custom Window Width=890 mm  [stored 2.91995 ft]; Energy Advantage SHGC Value=0.553; Energy Advantage U Value=5; Heavy Duty Interlocker=No; Height=1190 mm  [stored 3.9042 ft]; Intruderprufe LowE SHGC Value=0.512; Intruderprufe LowE U Value=4.76; Intruderprufe SHGC Value=0.584; Intruderprufe U Value=5.98; Is Heavy Duty Mullion=0 mm  [stored 0 ft]; Limit Sash Width Left Max=591 mm; Limit Sash Width Left Min=300 mm; Max Pane Area=0.36 m²; Sash Height=1133 mm; Sash Width Left=446 mm; Sash Width Right=446 mm; Standard Interlocker=Yes; Width=890 mm  [stored 2.91995 ft]; Windload Design=2000 mm  [stored 6.56168 ft]
- 1000SW-0915XO-1500Pa: Area Left Sash Glazing=0.46 m²; Area Right Sash Glazing=0.46 m²; Clearvue SHGC Value=0.635; Clearvue U Value=6.19; Custom Windload=1500 mm  [stored 4.92126 ft]; Custom Window Height=1490 mm  [stored 4.88845 ft]; Custom Window Width=890 mm  [stored 2.91995 ft]; Energy Advantage SHGC Value=0.57; Energy Advantage U Value=4.87; Heavy Duty Interlocker=No; Height=1490 mm  [stored 4.88845 ft]; Intruderprufe LowE SHGC Value=0.528; Intruderprufe LowE U Value=4.67; Intruderprufe SHGC Value=0.603; Intruderprufe U Value=5.94; Is Heavy Duty Mullion=0 mm  [stored 0 ft]; Limit Sash Width Left Max=591 mm; Limit Sash Width Left Min=300 mm; Max Pane Area=0.46 m²; Sash Height=1433 mm; Sash Width Left=446 mm; Sash Width Right=446 mm; Standard Interlocker=Yes; Width=890 mm  [stored 2.91995 ft]; Windload Design=1500 mm  [stored 4.92126 ft]
- 1000SW-0915XO-2000Pa: Area Left Sash Glazing=0.46 m²; Area Right Sash Glazing=0.46 m²; Clearvue SHGC Value=0.635; Clearvue U Value=6.19; Custom Windload=2000 mm  [stored 6.56168 ft]; Custom Window Height=1490 mm  [stored 4.88845 ft]; Custom Window Width=890 mm  [stored 2.91995 ft]; Energy Advantage SHGC Value=0.57; Energy Advantage U Value=4.87; Heavy Duty Interlocker=No; Height=1490 mm  [stored 4.88845 ft]; Intruderprufe LowE SHGC Value=0.528; Intruderprufe LowE U Value=4.67; Intruderprufe SHGC Value=0.603; Intruderprufe U Value=5.94; Is Heavy Duty Mullion=0 mm  [stored 0 ft]; Limit Sash Width Left Max=591 mm; Limit Sash Width Left Min=300 mm; Max Pane Area=0.46 m²; Sash Height=1433 mm; Sash Width Left=446 mm; Sash Width Right=446 mm; Standard Interlocker=Yes; Width=890 mm  [stored 2.91995 ft]; Windload Design=2000 mm  [stored 6.56168 ft]
- 1000SW-0918XO-1500Pa: Area Left Sash Glazing=0.56 m²; Area Right Sash Glazing=0.56 m²; Clearvue SHGC Value=0.648; Clearvue U Value=6.14; Custom Windload=1500 mm  [stored 4.92126 ft]; Custom Window Height=1790 mm  [stored 5.8727 ft]; Custom Window Width=890 mm  [stored 2.91995 ft]; Energy Advantage SHGC Value=0.581; Energy Advantage U Value=4.79; Heavy Duty Interlocker=Yes; Height=1790 mm  [stored 5.8727 ft]; Intruderprufe LowE SHGC Value=0.539; Intruderprufe LowE U Value=4.61; Intruderprufe SHGC Value=0.615; Intruderprufe U Value=5.91; Is Heavy Duty Mullion=1 mm  [stored 0.00328084 ft]; Limit Sash Width Left Max=591 mm; Limit Sash Width Left Min=300 mm; Max Pane Area=0.56 m²; Sash Height=1733 mm; Sash Width Left=446 mm; Sash Width Right=446 mm; Standard Interlocker=No; Width=890 mm  [stored 2.91995 ft]; Windload Design=1500 mm  [stored 4.92126 ft]
- 1000SW-0918XO-2000Pa: Area Left Sash Glazing=0.56 m²; Area Right Sash Glazing=0.56 m²; Clearvue SHGC Value=0.648; Clearvue U Value=6.14; Custom Windload=2000 mm  [stored 6.56168 ft]; Custom Window Height=1790 mm  [stored 5.8727 ft]; Custom Window Width=890 mm  [stored 2.91995 ft]; Energy Advantage SHGC Value=0.581; Energy Advantage U Value=4.79; Heavy Duty Interlocker=Yes; Height=1790 mm  [stored 5.8727 ft]; Intruderprufe LowE SHGC Value=0.539; Intruderprufe LowE U Value=4.61; Intruderprufe SHGC Value=0.615; Intruderprufe U Value=5.91; Is Heavy Duty Mullion=1 mm  [stored 0.00328084 ft]; Limit Sash Width Left Max=591 mm; Limit Sash Width Left Min=300 mm; Max Pane Area=0.56 m²; Sash Height=1733 mm; Sash Width Left=446 mm; Sash Width Right=446 mm; Standard Interlocker=No; Width=890 mm  [stored 2.91995 ft]; Windload Design=2000 mm  [stored 6.56168 ft]
- 1000SW-1206XO-1500Pa: Area Left Sash Glazing=0.21 m²; Area Right Sash Glazing=0.21 m²; Clearvue SHGC Value=0.546; Clearvue U Value=6.69; Custom Windload=1500 mm  [stored 4.92126 ft]; Custom Window Height=590 mm  [stored 1.9357 ft]; Custom Window Width=1190 mm  [stored 3.9042 ft]; Energy Advantage SHGC Value=0.491; Energy Advantage U Value=5.56; Heavy Duty Interlocker=No; Height=590 mm  [stored 1.9357 ft]; Intruderprufe LowE SHGC Value=0.449; Intruderprufe LowE U Value=5.14; Intruderprufe SHGC Value=0.515; Intruderprufe U Value=6.22; Is Heavy Duty Mullion=0 mm  [stored 0 ft]; Limit Sash Width Left Max=891 mm; Limit Sash Width Left Min=300 mm; Max Pane Area=0.21 m²; Sash Height=533 mm; Sash Width Left=596 mm; Sash Width Right=596 mm; Standard Interlocker=Yes; Width=1190 mm  [stored 3.9042 ft]; Windload Design=1500 mm  [stored 4.92126 ft]
- 1000SW-1206XO-2000Pa: Area Left Sash Glazing=0.21 m²; Area Right Sash Glazing=0.21 m²; Clearvue SHGC Value=0.546; Clearvue U Value=6.69; Custom Windload=2000 mm  [stored 6.56168 ft]; Custom Window Height=590 mm  [stored 1.9357 ft]; Custom Window Width=1190 mm  [stored 3.9042 ft]; Energy Advantage SHGC Value=0.491; Energy Advantage U Value=5.56; Heavy Duty Interlocker=No; Height=590 mm  [stored 1.9357 ft]; Intruderprufe LowE SHGC Value=0.449; Intruderprufe LowE U Value=5.14; Intruderprufe SHGC Value=0.515; Intruderprufe U Value=6.22; Is Heavy Duty Mullion=0 mm  [stored 0 ft]; Limit Sash Width Left Max=891 mm; Limit Sash Width Left Min=300 mm; Max Pane Area=0.21 m²; Sash Height=533 mm; Sash Width Left=596 mm; Sash Width Right=596 mm; Standard Interlocker=Yes; Width=1190 mm  [stored 3.9042 ft]; Windload Design=2000 mm  [stored 6.56168 ft]
- 1000SW-1209XO-1500Pa: Area Left Sash Glazing=0.36 m²; Area Right Sash Glazing=0.36 m²; Clearvue SHGC Value=0.614; Clearvue U Value=6.42; Custom Windload=1500 mm  [stored 4.92126 ft]; Custom Window Height=890 mm  [stored 2.91995 ft]; Custom Window Width=1190 mm  [stored 3.9042 ft]; Energy Advantage SHGC Value=0.55; Energy Advantage U Value=5.11; Heavy Duty Interlocker=No; Height=890 mm  [stored 2.91995 ft]; Intruderprufe LowE SHGC Value=0.507; Intruderprufe LowE U Value=4.8; Intruderprufe SHGC Value=0.58; Intruderprufe U Value=6.06; Is Heavy Duty Mullion=0 mm  [stored 0 ft]; Limit Sash Width Left Max=891 mm; Limit Sash Width Left Min=300 mm; Max Pane Area=0.36 m²; Sash Height=833 mm; Sash Width Left=596 mm; Sash Width Right=596 mm; Standard Interlocker=Yes; Width=1190 mm  [stored 3.9042 ft]; Windload Design=1500 mm  [stored 4.92126 ft]
- 1000SW-1209XO-2000Pa: Area Left Sash Glazing=0.36 m²; Area Right Sash Glazing=0.36 m²; Clearvue SHGC Value=0.614; Clearvue U Value=6.42; Custom Windload=2000 mm  [stored 6.56168 ft]; Custom Window Height=890 mm  [stored 2.91995 ft]; Custom Window Width=1190 mm  [stored 3.9042 ft]; Energy Advantage SHGC Value=0.55; Energy Advantage U Value=5.11; Heavy Duty Interlocker=No; Height=890 mm  [stored 2.91995 ft]; Intruderprufe LowE SHGC Value=0.507; Intruderprufe LowE U Value=4.8; Intruderprufe SHGC Value=0.58; Intruderprufe U Value=6.06; Is Heavy Duty Mullion=0 mm  [stored 0 ft]; Limit Sash Width Left Max=891 mm; Limit Sash Width Left Min=300 mm; Max Pane Area=0.36 m²; Sash Height=833 mm; Sash Width Left=596 mm; Sash Width Right=596 mm; Standard Interlocker=Yes; Width=1190 mm  [stored 3.9042 ft]; Windload Design=2000 mm  [stored 6.56168 ft]
- 1000SW-1212XO-1500Pa: Area Left Sash Glazing=0.51 m²; Area Right Sash Glazing=0.51 m²; Clearvue SHGC Value=0.647; Clearvue U Value=6.29; Custom Windload=1500 mm  [stored 4.92126 ft]; Custom Window Height=1190 mm  [stored 3.9042 ft]; Custom Window Width=1190 mm  [stored 3.9042 ft]; Energy Advantage SHGC Value=0.58; Energy Advantage U Value=4.88; Heavy Duty Interlocker=No; Height=1190 mm  [stored 3.9042 ft]; Intruderprufe LowE SHGC Value=0.536; Intruderprufe LowE U Value=4.63; Intruderprufe SHGC Value=0.613; Intruderprufe U Value=5.99; Is Heavy Duty Mullion=0 mm  [stored 0 ft]; Limit Sash Width Left Max=891 mm; Limit Sash Width Left Min=300 mm; Max Pane Area=0.51 m²; Sash Height=1133 mm; Sash Width Left=596 mm; Sash Width Right=596 mm; Standard Interlocker=Yes; Width=1190 mm  [stored 3.9042 ft]; Windload Design=1500 mm  [stored 4.92126 ft]
- 1000SW-1212XO-2000Pa: Area Left Sash Glazing=0.51 m²; Area Right Sash Glazing=0.51 m²; Clearvue SHGC Value=0.647; Clearvue U Value=6.29; Custom Windload=2000 mm  [stored 6.56168 ft]; Custom Window Height=1190 mm  [stored 3.9042 ft]; Custom Window Width=1190 mm  [stored 3.9042 ft]; Energy Advantage SHGC Value=0.58; Energy Advantage U Value=4.88; Heavy Duty Interlocker=No; Height=1190 mm  [stored 3.9042 ft]; Intruderprufe LowE SHGC Value=0.536; Intruderprufe LowE U Value=4.63; Intruderprufe SHGC Value=0.613; Intruderprufe U Value=5.99; Is Heavy Duty Mullion=0 mm  [stored 0 ft]; Limit Sash Width Left Max=891 mm; Limit Sash Width Left Min=300 mm; Max Pane Area=0.51 m²; Sash Height=1133 mm; Sash Width Left=596 mm; Sash Width Right=596 mm; Standard Interlocker=Yes; Width=1190 mm  [stored 3.9042 ft]; Windload Design=2000 mm  [stored 6.56168 ft]
- 1000SW-1215XO-1500Pa: Area Left Sash Glazing=0.66 m²; Area Right Sash Glazing=0.66 m²; Clearvue SHGC Value=0.667; Clearvue U Value=6.2; Custom Windload=1500 mm  [stored 4.92126 ft]; Custom Window Height=1490 mm  [stored 4.88845 ft]; Custom Window Width=1190 mm  [stored 3.9042 ft]; Energy Advantage SHGC Value=0.597; Energy Advantage U Value=4.74; Heavy Duty Interlocker=No; Height=1490 mm  [stored 4.88845 ft]; Intruderprufe LowE SHGC Value=0.553; Intruderprufe LowE U Value=4.53; Intruderprufe SHGC Value=0.632; Intruderprufe U Value=5.94; Is Heavy Duty Mullion=0 mm  [stored 0 ft]; Limit Sash Width Left Max=891 mm; Limit Sash Width Left Min=300 mm; Max Pane Area=0.66 m²; Sash Height=1433 mm; Sash Width Left=596 mm; Sash Width Right=596 mm; Standard Interlocker=Yes; Width=1190 mm  [stored 3.9042 ft]; Windload Design=1500 mm  [stored 4.92126 ft]
- 1000SW-1215XO-2000Pa: Area Left Sash Glazing=0.66 m²; Area Right Sash Glazing=0.66 m²; Clearvue SHGC Value=0.667; Clearvue U Value=6.2; Custom Windload=2000 mm  [stored 6.56168 ft]; Custom Window Height=1490 mm  [stored 4.88845 ft]; Custom Window Width=1190 mm  [stored 3.9042 ft]; Energy Advantage SHGC Value=0.597; Energy Advantage U Value=4.74; Heavy Duty Interlocker=No; Height=1490 mm  [stored 4.88845 ft]; Intruderprufe LowE SHGC Value=0.553; Intruderprufe LowE U Value=4.53; Intruderprufe SHGC Value=0.632; Intruderprufe U Value=5.94; Is Heavy Duty Mullion=0 mm  [stored 0 ft]; Limit Sash Width Left Max=891 mm; Limit Sash Width Left Min=300 mm; Max Pane Area=0.66 m²; Sash Height=1433 mm; Sash Width Left=596 mm; Sash Width Right=596 mm; Standard Interlocker=Yes; Width=1190 mm  [stored 3.9042 ft]; Windload Design=2000 mm  [stored 6.56168 ft]
- 1000SW-1218XO-1500Pa: Area Left Sash Glazing=0.81 m²; Area Right Sash Glazing=0.81 m²; Clearvue SHGC Value=0.68; Clearvue U Value=6.15; Custom Windload=1500 mm  [stored 4.92126 ft]; Custom Window Height=1790 mm  [stored 5.8727 ft]; Custom Window Width=1190 mm  [stored 3.9042 ft]; Energy Advantage SHGC Value=0.609; Energy Advantage U Value=4.65; Heavy Duty Interlocker=Yes; Height=1790 mm  [stored 5.8727 ft]; Intruderprufe LowE SHGC Value=0.565; Intruderprufe LowE U Value=4.46; Intruderprufe SHGC Value=0.645; Intruderprufe U Value=5.91; Is Heavy Duty Mullion=1 mm  [stored 0.00328084 ft]; Limit Sash Width Left Max=891 mm; Limit Sash Width Left Min=300 mm; Max Pane Area=0.81 m²; Sash Height=1733 mm; Sash Width Left=596 mm; Sash Width Right=596 mm; Standard Interlocker=No; Width=1190 mm  [stored 3.9042 ft]; Windload Design=1500 mm  [stored 4.92126 ft]
- 1000SW-1218XO-2000Pa: Area Left Sash Glazing=0.81 m²; Area Right Sash Glazing=0.81 m²; Clearvue SHGC Value=0.68; Clearvue U Value=6.15; Custom Windload=2000 mm  [stored 6.56168 ft]; Custom Window Height=1790 mm  [stored 5.8727 ft]; Custom Window Width=1190 mm  [stored 3.9042 ft]; Energy Advantage SHGC Value=0.609; Energy Advantage U Value=4.65; Heavy Duty Interlocker=Yes; Height=1790 mm  [stored 5.8727 ft]; Intruderprufe LowE SHGC Value=0.565; Intruderprufe LowE U Value=4.46; Intruderprufe SHGC Value=0.645; Intruderprufe U Value=5.91; Is Heavy Duty Mullion=1 mm  [stored 0.00328084 ft]; Limit Sash Width Left Max=891 mm; Limit Sash Width Left Min=300 mm; Max Pane Area=0.81 m²; Sash Height=1733 mm; Sash Width Left=596 mm; Sash Width Right=596 mm; Standard Interlocker=No; Width=1190 mm  [stored 3.9042 ft]; Windload Design=2000 mm  [stored 6.56168 ft]
- 1000SW-1506XO-1500Pa: Area Left Sash Glazing=0.28 m²; Area Right Sash Glazing=0.28 m²; Clearvue SHGC Value=0.562; Clearvue U Value=6.71; Custom Windload=1500 mm  [stored 4.92126 ft]; Custom Window Height=590 mm  [stored 1.9357 ft]; Custom Window Width=1490 mm  [stored 4.88845 ft]; Energy Advantage SHGC Value=0.505; Energy Advantage U Value=5.52; Heavy Duty Interlocker=No; Height=590 mm  [stored 1.9357 ft]; Intruderprufe LowE SHGC Value=0.461; Intruderprufe LowE U Value=5.08; Intruderprufe SHGC Value=0.529; Intruderprufe U Value=6.23; Is Heavy Duty Mullion=0 mm  [stored 0 ft]; Limit Sash Width Left Max=1191 mm; Limit Sash Width Left Min=300 mm; Max Pane Area=0.28 m²; Sash Height=533 mm; Sash Width Left=746 mm; Sash Width Right=746 mm; Standard Interlocker=Yes; Width=1490 mm  [stored 4.88845 ft]; Windload Design=1500 mm  [stored 4.92126 ft]
- 1000SW-1506XO-2000Pa: Area Left Sash Glazing=0.28 m²; Area Right Sash Glazing=0.28 m²; Clearvue SHGC Value=0.562; Clearvue U Value=6.71; Custom Windload=2000 mm  [stored 6.56168 ft]; Custom Window Height=590 mm  [stored 1.9357 ft]; Custom Window Width=1490 mm  [stored 4.88845 ft]; Energy Advantage SHGC Value=0.505; Energy Advantage U Value=5.52; Heavy Duty Interlocker=No; Height=590 mm  [stored 1.9357 ft]; Intruderprufe LowE SHGC Value=0.461; Intruderprufe LowE U Value=5.08; Intruderprufe SHGC Value=0.529; Intruderprufe U Value=6.23; Is Heavy Duty Mullion=0 mm  [stored 0 ft]; Limit Sash Width Left Max=1191 mm; Limit Sash Width Left Min=300 mm; Max Pane Area=0.28 m²; Sash Height=533 mm; Sash Width Left=746 mm; Sash Width Right=746 mm; Standard Interlocker=Yes; Width=1490 mm  [stored 4.88845 ft]; Windload Design=2000 mm  [stored 6.56168 ft]
- 1000SW-1509XO-1500Pa: Area Left Sash Glazing=0.47 m²; Area Right Sash Glazing=0.47 m²; Clearvue SHGC Value=0.631; Clearvue U Value=6.43; Custom Windload=1500 mm  [stored 4.92126 ft]; Custom Window Height=890 mm  [stored 2.91995 ft]; Custom Window Width=1490 mm  [stored 4.88845 ft]; Energy Advantage SHGC Value=0.565; Energy Advantage U Value=5.04; Heavy Duty Interlocker=No; Height=890 mm  [stored 2.91995 ft]; Intruderprufe LowE SHGC Value=0.521; Intruderprufe LowE U Value=4.73; Intruderprufe SHGC Value=0.596; Intruderprufe U Value=6.07; Is Heavy Duty Mullion=0 mm  [stored 0 ft]; Limit Sash Width Left Max=1191 mm; Limit Sash Width Left Min=300 mm; Max Pane Area=0.47 m²; Sash Height=833 mm; Sash Width Left=746 mm; Sash Width Right=746 mm; Standard Interlocker=Yes; Width=1490 mm  [stored 4.88845 ft]; Windload Design=1500 mm  [stored 4.92126 ft]
- 1000SW-1509XO-2000Pa: Area Left Sash Glazing=0.47 m²; Area Right Sash Glazing=0.47 m²; Clearvue SHGC Value=0.631; Clearvue U Value=6.43; Custom Windload=2000 mm  [stored 6.56168 ft]; Custom Window Height=890 mm  [stored 2.91995 ft]; Custom Window Width=1490 mm  [stored 4.88845 ft]; Energy Advantage SHGC Value=0.565; Energy Advantage U Value=5.04; Heavy Duty Interlocker=No; Height=890 mm  [stored 2.91995 ft]; Intruderprufe LowE SHGC Value=0.521; Intruderprufe LowE U Value=4.73; Intruderprufe SHGC Value=0.596; Intruderprufe U Value=6.07; Is Heavy Duty Mullion=0 mm  [stored 0 ft]; Limit Sash Width Left Max=1191 mm; Limit Sash Width Left Min=300 mm; Max Pane Area=0.47 m²; Sash Height=833 mm; Sash Width Left=746 mm; Sash Width Right=746 mm; Standard Interlocker=Yes; Width=1490 mm  [stored 4.88845 ft]; Windload Design=2000 mm  [stored 6.56168 ft]
- 1000SW-1512XO-1500Pa: Area Left Sash Glazing=0.67 m²; Area Right Sash Glazing=0.67 m²; Clearvue SHGC Value=0.665; Clearvue U Value=6.3; Custom Windload=1500 mm  [stored 4.92126 ft]; Custom Window Height=1190 mm  [stored 3.9042 ft]; Custom Window Width=1490 mm  [stored 4.88845 ft]; Energy Advantage SHGC Value=0.596; Energy Advantage U Value=4.81; Heavy Duty Interlocker=No; Height=1190 mm  [stored 3.9042 ft]; Intruderprufe LowE SHGC Value=0.55; Intruderprufe LowE U Value=4; Intruderprufe SHGC Value=0.629; Intruderprufe U Value=5.99; Is Heavy Duty Mullion=0 mm  [stored 0 ft]; Limit Sash Width Left Max=1191 mm; Limit Sash Width Left Min=300 mm; Max Pane Area=0.67 m²; Sash Height=1133 mm; Sash Width Left=746 mm; Sash Width Right=746 mm; Standard Interlocker=Yes; Width=1490 mm  [stored 4.88845 ft]; Windload Design=1500 mm  [stored 4.92126 ft]
- 1000SW-1512XO-2000Pa: Area Left Sash Glazing=0.67 m²; Area Right Sash Glazing=0.67 m²; Clearvue SHGC Value=0.665; Clearvue U Value=6.3; Custom Windload=2000 mm  [stored 6.56168 ft]; Custom Window Height=1190 mm  [stored 3.9042 ft]; Custom Window Width=1490 mm  [stored 4.88845 ft]; Energy Advantage SHGC Value=0.596; Energy Advantage U Value=4.81; Heavy Duty Interlocker=No; Height=1190 mm  [stored 3.9042 ft]; Intruderprufe LowE SHGC Value=0.55; Intruderprufe LowE U Value=4; Intruderprufe SHGC Value=0.629; Intruderprufe U Value=5.99; Is Heavy Duty Mullion=0 mm  [stored 0 ft]; Limit Sash Width Left Max=1191 mm; Limit Sash Width Left Min=300 mm; Max Pane Area=0.67 m²; Sash Height=1133 mm; Sash Width Left=746 mm; Sash Width Right=746 mm; Standard Interlocker=Yes; Width=1490 mm  [stored 4.88845 ft]; Windload Design=2000 mm  [stored 6.56168 ft]
- 1000SW-1515XO-1500Pa: Area Left Sash Glazing=0.86 m²; Area Right Sash Glazing=0.86 m²; Clearvue SHGC Value=0.685; Clearvue U Value=6.21; Custom Windload=1500 mm  [stored 4.92126 ft]; Custom Window Height=1490 mm  [stored 4.88845 ft]; Custom Window Width=1490 mm  [stored 4.88845 ft]; Energy Advantage SHGC Value=0.614; Energy Advantage U Value=4.66; Heavy Duty Interlocker=No; Height=1490 mm  [stored 4.88845 ft]; Intruderprufe LowE SHGC Value=0.568; Intruderprufe LowE U Value=4.45; Intruderprufe SHGC Value=0.649; Intruderprufe U Value=5.94; Is Heavy Duty Mullion=0 mm  [stored 0 ft]; Limit Sash Width Left Max=1191 mm; Limit Sash Width Left Min=300 mm; Max Pane Area=0.86 m²; Sash Height=1433 mm; Sash Width Left=746 mm; Sash Width Right=746 mm; Standard Interlocker=Yes; Width=1490 mm  [stored 4.88845 ft]; Windload Design=1500 mm  [stored 4.92126 ft]
- 1000SW-1515XO-2000Pa: Area Left Sash Glazing=0.86 m²; Area Right Sash Glazing=0.86 m²; Clearvue SHGC Value=0.685; Clearvue U Value=6.21; Custom Windload=2000 mm  [stored 6.56168 ft]; Custom Window Height=1490 mm  [stored 4.88845 ft]; Custom Window Width=1490 mm  [stored 4.88845 ft]; Energy Advantage SHGC Value=0.614; Energy Advantage U Value=4.66; Heavy Duty Interlocker=Yes; Height=1490 mm  [stored 4.88845 ft]; Intruderprufe LowE SHGC Value=0.568; Intruderprufe LowE U Value=4.45; Intruderprufe SHGC Value=0.649; Intruderprufe U Value=5.94; Is Heavy Duty Mullion=1 mm  [stored 0.00328084 ft]; Limit Sash Width Left Max=1191 mm; Limit Sash Width Left Min=300 mm; Max Pane Area=0.86 m²; Sash Height=1433 mm; Sash Width Left=746 mm; Sash Width Right=746 mm; Standard Interlocker=No; Width=1490 mm  [stored 4.88845 ft]; Windload Design=2000 mm  [stored 6.56168 ft]
- 1000SW-1518XO-1500Pa: Area Left Sash Glazing=1.05 m²; Area Right Sash Glazing=1.05 m²; Clearvue SHGC Value=0.699; Clearvue U Value=6.16; Custom Windload=1500 mm  [stored 4.92126 ft]; Custom Window Height=1790 mm  [stored 5.8727 ft]; Custom Window Width=1490 mm  [stored 4.88845 ft]; Energy Advantage SHGC Value=0.626; Energy Advantage U Value=4.57; Heavy Duty Interlocker=Yes; Height=1790 mm  [stored 5.8727 ft]; Intruderprufe LowE SHGC Value=0.58; Intruderprufe LowE U Value=4.38; Intruderprufe SHGC Value=0.662; Intruderprufe U Value=5.91; Is Heavy Duty Mullion=1 mm  [stored 0.00328084 ft]; Limit Sash Width Left Max=1191 mm; Limit Sash Width Left Min=300 mm; Max Pane Area=1.05 m²; Sash Height=1733 mm; Sash Width Left=746 mm; Sash Width Right=746 mm; Standard Interlocker=No; Width=1490 mm  [stored 4.88845 ft]; Windload Design=1500 mm  [stored 4.92126 ft]
- 1000SW-1518XO-2000Pa: Area Left Sash Glazing=1.05 m²; Area Right Sash Glazing=1.05 m²; Clearvue SHGC Value=0.699; Clearvue U Value=6.16; Custom Windload=2000 mm  [stored 6.56168 ft]; Custom Window Height=1790 mm  [stored 5.8727 ft]; Custom Window Width=1490 mm  [stored 4.88845 ft]; Energy Advantage SHGC Value=0.626; Energy Advantage U Value=4.57; Heavy Duty Interlocker=Yes; Height=1790 mm  [stored 5.8727 ft]; Intruderprufe LowE SHGC Value=0.58; Intruderprufe LowE U Value=4.38; Intruderprufe SHGC Value=0.662; Intruderprufe U Value=5.91; Is Heavy Duty Mullion=1 mm  [stored 0.00328084 ft]; Limit Sash Width Left Max=1191 mm; Limit Sash Width Left Min=300 mm; Max Pane Area=1.05 m²; Sash Height=1733 mm; Sash Width Left=746 mm; Sash Width Right=746 mm; Standard Interlocker=No; Width=1490 mm  [stored 4.88845 ft]; Windload Design=2000 mm  [stored 6.56168 ft]
- 1000SW-1806XO-1500Pa: Area Left Sash Glazing=0.34 m²; Area Right Sash Glazing=0.34 m²; Clearvue SHGC Value=0.572; Clearvue U Value=6.73; Custom Windload=1500 mm  [stored 4.92126 ft]; Custom Window Height=590 mm  [stored 1.9357 ft]; Custom Window Width=1790 mm  [stored 5.8727 ft]; Energy Advantage SHGC Value=0.513; Energy Advantage U Value=5.49; Heavy Duty Interlocker=No; Height=590 mm  [stored 1.9357 ft]; Intruderprufe LowE SHGC Value=4.69; Intruderprufe LowE U Value=5.05; Intruderprufe SHGC Value=0.539; Intruderprufe U Value=6.24; Is Heavy Duty Mullion=0 mm  [stored 0 ft]; Limit Sash Width Left Max=1491 mm; Limit Sash Width Left Min=300 mm; Max Pane Area=0.34 m²; Sash Height=533 mm; Sash Width Left=896 mm; Sash Width Right=896 mm; Standard Interlocker=Yes; Width=1790 mm  [stored 5.8727 ft]; Windload Design=1500 mm  [stored 4.92126 ft]
- 1000SW-1806XO-2000Pa: Area Left Sash Glazing=0.34 m²; Area Right Sash Glazing=0.34 m²; Clearvue SHGC Value=0.572; Clearvue U Value=6.73; Custom Windload=2000 mm  [stored 6.56168 ft]; Custom Window Height=590 mm  [stored 1.9357 ft]; Custom Window Width=1790 mm  [stored 5.8727 ft]; Energy Advantage SHGC Value=0.513; Energy Advantage U Value=5.49; Heavy Duty Interlocker=No; Height=590 mm  [stored 1.9357 ft]; Intruderprufe LowE SHGC Value=4.69; Intruderprufe LowE U Value=5.05; Intruderprufe SHGC Value=0.539; Intruderprufe U Value=6.24; Is Heavy Duty Mullion=0 mm  [stored 0 ft]; Limit Sash Width Left Max=1491 mm; Limit Sash Width Left Min=300 mm; Max Pane Area=0.34 m²; Sash Height=533 mm; Sash Width Left=896 mm; Sash Width Right=896 mm; Standard Interlocker=Yes; Width=1790 mm  [stored 5.8727 ft]; Windload Design=2000 mm  [stored 6.56168 ft]
- 1000SW-1809XO-1500Pa: Area Left Sash Glazing=0.58 m²; Area Right Sash Glazing=0.58 m²; Clearvue SHGC Value=0.642; Clearvue U Value=6.44; Custom Windload=1500 mm  [stored 4.92126 ft]; Custom Window Height=890 mm  [stored 2.91995 ft]; Custom Window Width=1790 mm  [stored 5.8727 ft]; Energy Advantage SHGC Value=0.575; Energy Advantage U Value=5; Heavy Duty Interlocker=No; Height=890 mm  [stored 2.91995 ft]; Intruderprufe LowE SHGC Value=0.53; Intruderprufe LowE U Value=4.68; Intruderprufe SHGC Value=0.607; Intruderprufe U Value=6.08; Is Heavy Duty Mullion=0 mm  [stored 0 ft]; Limit Sash Width Left Max=1491 mm; Limit Sash Width Left Min=300 mm; Max Pane Area=0.58 m²; Sash Height=833 mm; Sash Width Left=896 mm; Sash Width Right=896 mm; Standard Interlocker=Yes; Width=1790 mm  [stored 5.8727 ft]; Windload Design=1500 mm  [stored 4.92126 ft]
- 1000SW-1809XO-2000Pa: Area Left Sash Glazing=0.58 m²; Area Right Sash Glazing=0.58 m²; Clearvue SHGC Value=0.642; Clearvue U Value=6.44; Custom Windload=2000 mm  [stored 6.56168 ft]; Custom Window Height=890 mm  [stored 2.91995 ft]; Custom Window Width=1790 mm  [stored 5.8727 ft]; Energy Advantage SHGC Value=0.575; Energy Advantage U Value=5; Heavy Duty Interlocker=No; Height=890 mm  [stored 2.91995 ft]; Intruderprufe LowE SHGC Value=0.53; Intruderprufe LowE U Value=4.68; Intruderprufe SHGC Value=0.607; Intruderprufe U Value=6.08; Is Heavy Duty Mullion=0 mm  [stored 0 ft]; Limit Sash Width Left Max=1491 mm; Limit Sash Width Left Min=300 mm; Max Pane Area=0.58 m²; Sash Height=833 mm; Sash Width Left=896 mm; Sash Width Right=896 mm; Standard Interlocker=Yes; Width=1790 mm  [stored 5.8727 ft]; Windload Design=2000 mm  [stored 6.56168 ft]
- 1000SW-1812XO-1500Pa: Area Left Sash Glazing=0.82 m²; Area Right Sash Glazing=0.82 m²; Clearvue SHGC Value=0.677; Clearvue U Value=6.3; Custom Windload=1500 mm  [stored 4.92126 ft]; Custom Window Height=1190 mm  [stored 3.9042 ft]; Custom Window Width=1790 mm  [stored 5.8727 ft]; Energy Advantage SHGC Value=0.606; Energy Advantage U Value=4.76; Heavy Duty Interlocker=No; Height=1190 mm  [stored 3.9042 ft]; Intruderprufe LowE SHGC Value=0.56; Intruderprufe LowE U Value=4.5; Intruderprufe SHGC Value=0.641; Intruderprufe U Value=5.99; Is Heavy Duty Mullion=0 mm  [stored 0 ft]; Limit Sash Width Left Max=1491 mm; Limit Sash Width Left Min=300 mm; Max Pane Area=0.82 m²; Sash Height=1133 mm; Sash Width Left=896 mm; Sash Width Right=896 mm; Standard Interlocker=Yes; Width=1790 mm  [stored 5.8727 ft]; Windload Design=1500 mm  [stored 4.92126 ft]
- 1000SW-1812XO-2000Pa: Area Left Sash Glazing=0.82 m²; Area Right Sash Glazing=0.82 m²; Clearvue SHGC Value=0.677; Clearvue U Value=6.3; Custom Windload=2000 mm  [stored 6.56168 ft]; Custom Window Height=1190 mm  [stored 3.9042 ft]; Custom Window Width=1790 mm  [stored 5.8727 ft]; Energy Advantage SHGC Value=0.606; Energy Advantage U Value=4.76; Heavy Duty Interlocker=No; Height=1190 mm  [stored 3.9042 ft]; Intruderprufe LowE SHGC Value=0.56; Intruderprufe LowE U Value=4.5; Intruderprufe SHGC Value=0.641; Intruderprufe U Value=5.99; Is Heavy Duty Mullion=0 mm  [stored 0 ft]; Limit Sash Width Left Max=1491 mm; Limit Sash Width Left Min=300 mm; Max Pane Area=0.82 m²; Sash Height=1133 mm; Sash Width Left=896 mm; Sash Width Right=896 mm; Standard Interlocker=Yes; Width=1790 mm  [stored 5.8727 ft]; Windload Design=2000 mm  [stored 6.56168 ft]
- 1000SW-1815XO-1500Pa: Area Left Sash Glazing=1.06 m²; Area Right Sash Glazing=1.06 m²; Clearvue SHGC Value=0.693; Clearvue U Value=6.22; Custom Windload=1500 mm  [stored 4.92126 ft]; Custom Window Height=1490 mm  [stored 4.88845 ft]; Custom Window Width=1790 mm  [stored 5.8727 ft]; Energy Advantage SHGC Value=0.625; Energy Advantage U Value=4.61; Heavy Duty Interlocker=Yes; Height=1490 mm  [stored 4.88845 ft]; Intruderprufe LowE SHGC Value=0.578; Intruderprufe LowE U Value=4.39; Intruderprufe SHGC Value=0.661; Intruderprufe U Value=5.95; Is Heavy Duty Mullion=1 mm  [stored 0.00328084 ft]; Limit Sash Width Left Max=1491 mm; Limit Sash Width Left Min=300 mm; Max Pane Area=1.06 m²; Sash Height=1433 mm; Sash Width Left=896 mm; Sash Width Right=896 mm; Standard Interlocker=No; Width=1790 mm  [stored 5.8727 ft]; Windload Design=1500 mm  [stored 4.92126 ft]
- 1000SW-1815XO-2000Pa: Area Left Sash Glazing=1.06 m²; Area Right Sash Glazing=1.06 m²; Clearvue SHGC Value=0.693; Clearvue U Value=6.22; Custom Windload=2000 mm  [stored 6.56168 ft]; Custom Window Height=1490 mm  [stored 4.88845 ft]; Custom Window Width=1790 mm  [stored 5.8727 ft]; Energy Advantage SHGC Value=0.625; Energy Advantage U Value=4.61; Heavy Duty Interlocker=Yes; Height=1490 mm  [stored 4.88845 ft]; Intruderprufe LowE SHGC Value=0.578; Intruderprufe LowE U Value=4.39; Intruderprufe SHGC Value=0.661; Intruderprufe U Value=5.95; Is Heavy Duty Mullion=1 mm  [stored 0.00328084 ft]; Limit Sash Width Left Max=1491 mm; Limit Sash Width Left Min=300 mm; Max Pane Area=1.06 m²; Sash Height=1433 mm; Sash Width Left=896 mm; Sash Width Right=896 mm; Standard Interlocker=No; Width=1790 mm  [stored 5.8727 ft]; Windload Design=2000 mm  [stored 6.56168 ft]
- 1000SW-1818XO-1500Pa: Area Left Sash Glazing=1.3 m²; Area Right Sash Glazing=1.3 m²; Clearvue SHGC Value=0.712; Clearvue U Value=6.16; Custom Windload=1500 mm  [stored 4.92126 ft]; Custom Window Height=1790 mm  [stored 5.8727 ft]; Custom Window Width=1790 mm  [stored 5.8727 ft]; Energy Advantage SHGC Value=0.637; Energy Advantage U Value=4.52; Heavy Duty Interlocker=Yes; Height=1790 mm  [stored 5.8727 ft]; Intruderprufe LowE SHGC Value=0.59; Intruderprufe LowE U Value=4.32; Intruderprufe SHGC Value=0.674; Intruderprufe U Value=5.91; Is Heavy Duty Mullion=1 mm  [stored 0.00328084 ft]; Limit Sash Width Left Max=1491 mm; Limit Sash Width Left Min=300 mm; Max Pane Area=1.3 m²; Sash Height=1733 mm; Sash Width Left=896 mm; Sash Width Right=896 mm; Standard Interlocker=No; Width=1790 mm  [stored 5.8727 ft]; Windload Design=1500 mm  [stored 4.92126 ft]
- 1000SW-1818XO-2000Pa: Area Left Sash Glazing=1.3 m²; Area Right Sash Glazing=1.3 m²; Clearvue SHGC Value=0.712; Clearvue U Value=6.16; Custom Windload=2000 mm  [stored 6.56168 ft]; Custom Window Height=1790 mm  [stored 5.8727 ft]; Custom Window Width=1790 mm  [stored 5.8727 ft]; Energy Advantage SHGC Value=0.637; Energy Advantage U Value=4.52; Heavy Duty Interlocker=Yes; Height=1790 mm  [stored 5.8727 ft]; Intruderprufe LowE SHGC Value=0.59; Intruderprufe LowE U Value=4.32; Intruderprufe SHGC Value=0.674; Intruderprufe U Value=5.91; Is Heavy Duty Mullion=1 mm  [stored 0.00328084 ft]; Limit Sash Width Left Max=1491 mm; Limit Sash Width Left Min=300 mm; Max Pane Area=1.3 m²; Sash Height=1733 mm; Sash Width Left=896 mm; Sash Width Right=896 mm; Standard Interlocker=No; Width=1790 mm  [stored 5.8727 ft]; Windload Design=2000 mm  [stored 6.56168 ft]
- 1000SW-2106XO-1500Pa: Area Left Sash Glazing=0.41 m²; Area Right Sash Glazing=0.41 m²; Clearvue SHGC Value=0.579; Clearvue U Value=6.74; Custom Windload=1500 mm  [stored 4.92126 ft]; Custom Window Height=590 mm  [stored 1.9357 ft]; Custom Window Width=2090 mm  [stored 6.85696 ft]; Energy Advantage SHGC Value=0.52; Energy Advantage U Value=5.47; Heavy Duty Interlocker=No; Height=590 mm  [stored 1.9357 ft]; Intruderprufe LowE SHGC Value=0.474; Intruderprufe LowE U Value=5.02; Intruderprufe SHGC Value=0.545; Intruderprufe U Value=6.24; Is Heavy Duty Mullion=0 mm  [stored 0 ft]; Limit Sash Width Left Max=1500 mm  [stored 4.92126 ft]; Limit Sash Width Left Min=591 mm; Max Pane Area=0.41 m²; Sash Height=533 mm; Sash Width Left=1046 mm; Sash Width Right=1046 mm; Standard Interlocker=Yes; Width=2090 mm  [stored 6.85696 ft]; Windload Design=1500 mm  [stored 4.92126 ft]
- 1000SW-2106XO-2000Pa: Area Left Sash Glazing=0.41 m²; Area Right Sash Glazing=0.41 m²; Clearvue SHGC Value=0.579; Clearvue U Value=6.74; Custom Windload=2000 mm  [stored 6.56168 ft]; Custom Window Height=590 mm  [stored 1.9357 ft]; Custom Window Width=2090 mm  [stored 6.85696 ft]; Energy Advantage SHGC Value=0.52; Energy Advantage U Value=5.47; Heavy Duty Interlocker=No; Height=590 mm  [stored 1.9357 ft]; Intruderprufe LowE SHGC Value=0.474; Intruderprufe LowE U Value=5.02; Intruderprufe SHGC Value=0.545; Intruderprufe U Value=6.24; Is Heavy Duty Mullion=0 mm  [stored 0 ft]; Limit Sash Width Left Max=1500 mm  [stored 4.92126 ft]; Limit Sash Width Left Min=591 mm; Max Pane Area=0.41 m²; Sash Height=533 mm; Sash Width Left=1046 mm; Sash Width Right=1046 mm; Standard Interlocker=Yes; Width=2090 mm  [stored 6.85696 ft]; Windload Design=2000 mm  [stored 6.56168 ft]
- 1000SW-2109XO-1500Pa: Area Left Sash Glazing=0.69 m²; Area Right Sash Glazing=0.69 m²; Clearvue SHGC Value=0.65; Clearvue U Value=6.45; Custom Windload=1500 mm  [stored 4.92126 ft]; Custom Window Height=890 mm  [stored 2.91995 ft]; Custom Window Width=2090 mm  [stored 6.85696 ft]; Energy Advantage SHGC Value=0.583; Energy Advantage U Value=4.97; Heavy Duty Interlocker=No; Height=890 mm  [stored 2.91995 ft]; Intruderprufe LowE SHGC Value=0.536; Intruderprufe LowE U Value=4.65; Intruderprufe SHGC Value=0.614; Intruderprufe U Value=6.08; Is Heavy Duty Mullion=0 mm  [stored 0 ft]; Limit Sash Width Left Max=1500 mm  [stored 4.92126 ft]; Limit Sash Width Left Min=591 mm; Max Pane Area=0.69 m²; Sash Height=833 mm; Sash Width Left=1046 mm; Sash Width Right=1046 mm; Standard Interlocker=Yes; Width=2090 mm  [stored 6.85696 ft]; Windload Design=1500 mm  [stored 4.92126 ft]
- 1000SW-2109XO-2000Pa: Area Left Sash Glazing=0.69 m²; Area Right Sash Glazing=0.69 m²; Clearvue SHGC Value=0.65; Clearvue U Value=6.45; Custom Windload=2000 mm  [stored 6.56168 ft]; Custom Window Height=890 mm  [stored 2.91995 ft]; Custom Window Width=2090 mm  [stored 6.85696 ft]; Energy Advantage SHGC Value=0.583; Energy Advantage U Value=4.97; Heavy Duty Interlocker=No; Height=890 mm  [stored 2.91995 ft]; Intruderprufe LowE SHGC Value=0.536; Intruderprufe LowE U Value=4.65; Intruderprufe SHGC Value=0.614; Intruderprufe U Value=6.08; Is Heavy Duty Mullion=0 mm  [stored 0 ft]; Limit Sash Width Left Max=1500 mm  [stored 4.92126 ft]; Limit Sash Width Left Min=591 mm; Max Pane Area=0.69 m²; Sash Height=833 mm; Sash Width Left=1046 mm; Sash Width Right=1046 mm; Standard Interlocker=Yes; Width=2090 mm  [stored 6.85696 ft]; Windload Design=2000 mm  [stored 6.56168 ft]
- 1000SW-2112XO-1500Pa: Area Left Sash Glazing=0.98 m²; Area Right Sash Glazing=0.98 m²; Clearvue SHGC Value=0.686; Clearvue U Value=6.31; Custom Windload=1500 mm  [stored 4.92126 ft]; Custom Window Height=1190 mm  [stored 3.9042 ft]; Custom Window Width=2090 mm  [stored 6.85696 ft]; Energy Advantage SHGC Value=0.614; Energy Advantage U Value=4.72; Heavy Duty Interlocker=No; Height=1190 mm  [stored 3.9042 ft]; Intruderprufe LowE SHGC Value=0.567; Intruderprufe LowE U Value=4.46; Intruderprufe SHGC Value=0.649; Intruderprufe U Value=6; Is Heavy Duty Mullion=0 mm  [stored 0 ft]; Limit Sash Width Left Max=1500 mm  [stored 4.92126 ft]; Limit Sash Width Left Min=591 mm; Max Pane Area=0.98 m²; Sash Height=1133 mm; Sash Width Left=1046 mm; Sash Width Right=1046 mm; Standard Interlocker=Yes; Width=2090 mm  [stored 6.85696 ft]; Windload Design=1500 mm  [stored 4.92126 ft]
- 1000SW-2112XO-2000Pa: Area Left Sash Glazing=0.98 m²; Area Right Sash Glazing=0.98 m²; Clearvue SHGC Value=0.686; Clearvue U Value=6.31; Custom Windload=2000 mm  [stored 6.56168 ft]; Custom Window Height=1190 mm  [stored 3.9042 ft]; Custom Window Width=2090 mm  [stored 6.85696 ft]; Energy Advantage SHGC Value=0.614; Energy Advantage U Value=4.72; Heavy Duty Interlocker=No; Height=1190 mm  [stored 3.9042 ft]; Intruderprufe LowE SHGC Value=0.567; Intruderprufe LowE U Value=4.46; Intruderprufe SHGC Value=0.649; Intruderprufe U Value=6; Is Heavy Duty Mullion=0 mm  [stored 0 ft]; Limit Sash Width Left Max=1500 mm  [stored 4.92126 ft]; Limit Sash Width Left Min=591 mm; Max Pane Area=0.98 m²; Sash Height=1133 mm; Sash Width Left=1046 mm; Sash Width Right=1046 mm; Standard Interlocker=Yes; Width=2090 mm  [stored 6.85696 ft]; Windload Design=2000 mm  [stored 6.56168 ft]
- 1000SW-2115XO-1500Pa: Area Left Sash Glazing=1.26 m²; Area Right Sash Glazing=1.26 m²; Clearvue SHGC Value=0.707; Clearvue U Value=6.22; Custom Windload=1500 mm  [stored 4.92126 ft]; Custom Window Height=1490 mm  [stored 4.88845 ft]; Custom Window Width=2090 mm  [stored 6.85696 ft]; Energy Advantage SHGC Value=0.632; Energy Advantage U Value=6.32; Heavy Duty Interlocker=Yes; Height=1490 mm  [stored 4.88845 ft]; Intruderprufe LowE SHGC Value=0.585; Intruderprufe LowE U Value=4.35; Intruderprufe SHGC Value=0.669; Intruderprufe U Value=5.95; Is Heavy Duty Mullion=1 mm  [stored 0.00328084 ft]; Limit Sash Width Left Max=1500 mm  [stored 4.92126 ft]; Limit Sash Width Left Min=591 mm; Max Pane Area=1.26 m²; Sash Height=1433 mm; Sash Width Left=1046 mm; Sash Width Right=1046 mm; Standard Interlocker=No; Width=2090 mm  [stored 6.85696 ft]; Windload Design=1500 mm  [stored 4.92126 ft]
- 1000SW-2115XO-2000Pa: Area Left Sash Glazing=1.26 m²; Area Right Sash Glazing=1.26 m²; Clearvue SHGC Value=0.707; Clearvue U Value=6.22; Custom Windload=2000 mm  [stored 6.56168 ft]; Custom Window Height=1490 mm  [stored 4.88845 ft]; Custom Window Width=2090 mm  [stored 6.85696 ft]; Energy Advantage SHGC Value=0.632; Energy Advantage U Value=6.32; Heavy Duty Interlocker=Yes; Height=1490 mm  [stored 4.88845 ft]; Intruderprufe LowE SHGC Value=0.585; Intruderprufe LowE U Value=4.35; Intruderprufe SHGC Value=0.669; Intruderprufe U Value=5.95; Is Heavy Duty Mullion=1 mm  [stored 0.00328084 ft]; Limit Sash Width Left Max=1500 mm  [stored 4.92126 ft]; Limit Sash Width Left Min=591 mm; Max Pane Area=1.26 m²; Sash Height=1433 mm; Sash Width Left=1046 mm; Sash Width Right=1046 mm; Standard Interlocker=No; Width=2090 mm  [stored 6.85696 ft]; Windload Design=2000 mm  [stored 6.56168 ft]
- 1000SW-2118XO-1500Pa: Area Left Sash Glazing=1.54 m²; Area Right Sash Glazing=1.54 m²; Clearvue SHGC Value=0.721; Clearvue U Value=6.16; Custom Windload=1500 mm  [stored 4.92126 ft]; Custom Window Height=1790 mm  [stored 5.8727 ft]; Custom Window Width=2090 mm  [stored 6.85696 ft]; Energy Advantage SHGC Value=0.645; Energy Advantage U Value=4.48; Heavy Duty Interlocker=Yes; Height=1790 mm  [stored 5.8727 ft]; Intruderprufe LowE SHGC Value=0.597; Intruderprufe LowE U Value=4.28; Intruderprufe SHGC Value=0.683; Intruderprufe U Value=5.92; Is Heavy Duty Mullion=1 mm  [stored 0.00328084 ft]; Limit Sash Width Left Max=1500 mm  [stored 4.92126 ft]; Limit Sash Width Left Min=591 mm; Max Pane Area=1.54 m²; Sash Height=1733 mm; Sash Width Left=1046 mm; Sash Width Right=1046 mm; Standard Interlocker=No; Width=2090 mm  [stored 6.85696 ft]; Windload Design=1500 mm  [stored 4.92126 ft]
- 1000SW-2118XO-2000Pa: Area Left Sash Glazing=1.54 m²; Area Right Sash Glazing=1.54 m²; Clearvue SHGC Value=0.721; Clearvue U Value=6.16; Custom Windload=2000 mm  [stored 6.56168 ft]; Custom Window Height=1790 mm  [stored 5.8727 ft]; Custom Window Width=2090 mm  [stored 6.85696 ft]; Energy Advantage SHGC Value=0.645; Energy Advantage U Value=4.48; Heavy Duty Interlocker=Yes; Height=1790 mm  [stored 5.8727 ft]; Intruderprufe LowE SHGC Value=0.597; Intruderprufe LowE U Value=4.28; Intruderprufe SHGC Value=0.683; Intruderprufe U Value=5.92; Is Heavy Duty Mullion=1 mm  [stored 0.00328084 ft]; Limit Sash Width Left Max=1500 mm  [stored 4.92126 ft]; Limit Sash Width Left Min=591 mm; Max Pane Area=1.54 m²; Sash Height=1733 mm; Sash Width Left=1046 mm; Sash Width Right=1046 mm; Standard Interlocker=No; Width=2090 mm  [stored 6.85696 ft]; Windload Design=2000 mm  [stored 6.56168 ft]
- 1000SW-2406XO-1500Pa: Area Left Sash Glazing=0.47 m²; Area Right Sash Glazing=0.47 m²; Clearvue SHGC Value=0.584; Clearvue U Value=6.75; Custom Windload=1500 mm  [stored 4.92126 ft]; Custom Window Height=590 mm  [stored 1.9357 ft]; Custom Window Width=2390 mm  [stored 7.84121 ft]; Energy Advantage SHGC Value=0.524; Energy Advantage U Value=5.46; Heavy Duty Interlocker=No; Height=590 mm  [stored 1.9357 ft]; Intruderprufe LowE SHGC Value=0.479; Intruderprufe LowE U Value=5; Intruderprufe SHGC Value=0.55; Intruderprufe U Value=6.25; Is Heavy Duty Mullion=0 mm  [stored 0 ft]; Limit Sash Width Left Max=1500 mm  [stored 4.92126 ft]; Limit Sash Width Left Min=891 mm; Max Pane Area=0.47 m²; Sash Height=533 mm; Sash Width Left=1196 mm; Sash Width Right=1196 mm; Standard Interlocker=Yes; Width=2390 mm  [stored 7.84121 ft]; Windload Design=1500 mm  [stored 4.92126 ft]
- 1000SW-2406XO-2000Pa: Area Left Sash Glazing=0.47 m²; Area Right Sash Glazing=0.47 m²; Clearvue SHGC Value=0.584; Clearvue U Value=6.75; Custom Windload=2000 mm  [stored 6.56168 ft]; Custom Window Height=590 mm  [stored 1.9357 ft]; Custom Window Width=2390 mm  [stored 7.84121 ft]; Energy Advantage SHGC Value=0.524; Energy Advantage U Value=5.46; Heavy Duty Interlocker=No; Height=590 mm  [stored 1.9357 ft]; Intruderprufe LowE SHGC Value=0.479; Intruderprufe LowE U Value=5; Intruderprufe SHGC Value=0.55; Intruderprufe U Value=6.25; Is Heavy Duty Mullion=0 mm  [stored 0 ft]; Limit Sash Width Left Max=1500 mm  [stored 4.92126 ft]; Limit Sash Width Left Min=891 mm; Max Pane Area=0.47 m²; Sash Height=533 mm; Sash Width Left=1196 mm; Sash Width Right=1196 mm; Standard Interlocker=Yes; Width=2390 mm  [stored 7.84121 ft]; Windload Design=2000 mm  [stored 6.56168 ft]
- 1000SW-2409XO-1500Pa: Area Left Sash Glazing=0.8 m²; Area Right Sash Glazing=0.8 m²; Clearvue SHGC Value=0.656; Clearvue U Value=6.45; Custom Windload=1500 mm  [stored 4.92126 ft]; Custom Window Height=890 mm  [stored 2.91995 ft]; Custom Window Width=2390 mm  [stored 7.84121 ft]; Energy Advantage SHGC Value=0.588; Energy Advantage U Value=4.95; Heavy Duty Interlocker=No; Height=890 mm  [stored 2.91995 ft]; Intruderprufe LowE SHGC Value=0.541; Intruderprufe LowE U Value=4.62; Intruderprufe SHGC Value=0.62; Intruderprufe U Value=6.08; Is Heavy Duty Mullion=0 mm  [stored 0 ft]; Limit Sash Width Left Max=1500 mm  [stored 4.92126 ft]; Limit Sash Width Left Min=891 mm; Max Pane Area=0.8 m²; Sash Height=833 mm; Sash Width Left=1196 mm; Sash Width Right=1196 mm; Standard Interlocker=Yes; Width=2390 mm  [stored 7.84121 ft]; Windload Design=1500 mm  [stored 4.92126 ft]
- 1000SW-2409XO-2000Pa: Area Left Sash Glazing=0.8 m²; Area Right Sash Glazing=0.8 m²; Clearvue SHGC Value=0.656; Clearvue U Value=6.45; Custom Windload=2000 mm  [stored 6.56168 ft]; Custom Window Height=890 mm  [stored 2.91995 ft]; Custom Window Width=2390 mm  [stored 7.84121 ft]; Energy Advantage SHGC Value=0.588; Energy Advantage U Value=4.95; Heavy Duty Interlocker=No; Height=890 mm  [stored 2.91995 ft]; Intruderprufe LowE SHGC Value=0.541; Intruderprufe LowE U Value=4.62; Intruderprufe SHGC Value=0.62; Intruderprufe U Value=6.08; Is Heavy Duty Mullion=0 mm  [stored 0 ft]; Limit Sash Width Left Max=1500 mm  [stored 4.92126 ft]; Limit Sash Width Left Min=891 mm; Max Pane Area=0.8 m²; Sash Height=833 mm; Sash Width Left=1196 mm; Sash Width Right=1196 mm; Standard Interlocker=Yes; Width=2390 mm  [stored 7.84121 ft]; Windload Design=2000 mm  [stored 6.56168 ft]
- 1000SW-2412XO-1500Pa: Area Left Sash Glazing=1.13 m²; Area Right Sash Glazing=1.13 m²; Clearvue SHGC Value=0.692; Clearvue U Value=6.31; Custom Windload=1500 mm  [stored 4.92126 ft]; Custom Window Height=1190 mm  [stored 3.9042 ft]; Custom Window Width=2390 mm  [stored 7.84121 ft]; Energy Advantage SHGC Value=0.619; Energy Advantage U Value=4.7; Heavy Duty Interlocker=No; Height=1190 mm  [stored 3.9042 ft]; Intruderprufe LowE SHGC Value=0.572; Intruderprufe LowE U Value=4.44; Intruderprufe SHGC Value=0.655; Intruderprufe U Value=6; Is Heavy Duty Mullion=0 mm  [stored 0 ft]; Limit Sash Width Left Max=1500 mm  [stored 4.92126 ft]; Limit Sash Width Left Min=891 mm; Max Pane Area=1.13 m²; Sash Height=1133 mm; Sash Width Left=1196 mm; Sash Width Right=1196 mm; Standard Interlocker=Yes; Width=2390 mm  [stored 7.84121 ft]; Windload Design=1500 mm  [stored 4.92126 ft]
- 1000SW-2412XO-2000Pa: Area Left Sash Glazing=1.13 m²; Area Right Sash Glazing=1.13 m²; Clearvue SHGC Value=0.692; Clearvue U Value=6.31; Custom Windload=2000 mm  [stored 6.56168 ft]; Custom Window Height=1190 mm  [stored 3.9042 ft]; Custom Window Width=2390 mm  [stored 7.84121 ft]; Energy Advantage SHGC Value=0.619; Energy Advantage U Value=4.7; Heavy Duty Interlocker=No; Height=1190 mm  [stored 3.9042 ft]; Intruderprufe LowE SHGC Value=0.572; Intruderprufe LowE U Value=4.44; Intruderprufe SHGC Value=0.655; Intruderprufe U Value=6; Is Heavy Duty Mullion=0 mm  [stored 0 ft]; Limit Sash Width Left Max=1500 mm  [stored 4.92126 ft]; Limit Sash Width Left Min=891 mm; Max Pane Area=1.13 m²; Sash Height=1133 mm; Sash Width Left=1196 mm; Sash Width Right=1196 mm; Standard Interlocker=Yes; Width=2390 mm  [stored 7.84121 ft]; Windload Design=2000 mm  [stored 6.56168 ft]
- 1000SW-2415XO-1500Pa: Area Left Sash Glazing=1.46 m²; Area Right Sash Glazing=1.46 m²; Clearvue SHGC Value=0.713; Clearvue U Value=6.22; Custom Windload=1500 mm  [stored 4.92126 ft]; Custom Window Height=1490 mm  [stored 4.88845 ft]; Custom Window Width=2390 mm  [stored 7.84121 ft]; Energy Advantage SHGC Value=0.638; Energy Advantage U Value=4.55; Heavy Duty Interlocker=Yes; Height=1490 mm  [stored 4.88845 ft]; Intruderprufe LowE SHGC Value=0.59; Intruderprufe LowE U Value=4.33; Intruderprufe SHGC Value=0.675; Intruderprufe U Value=5.95; Is Heavy Duty Mullion=1 mm  [stored 0.00328084 ft]; Limit Sash Width Left Max=1500 mm  [stored 4.92126 ft]; Limit Sash Width Left Min=891 mm; Max Pane Area=1.46 m²; Sash Height=1433 mm; Sash Width Left=1196 mm; Sash Width Right=1196 mm; Standard Interlocker=No; Width=2390 mm  [stored 7.84121 ft]; Windload Design=1500 mm  [stored 4.92126 ft]
- 1000SW-2415XO-2000Pa: Area Left Sash Glazing=1.46 m²; Area Right Sash Glazing=1.46 m²; Clearvue SHGC Value=0.713; Clearvue U Value=6.22; Custom Windload=2000 mm  [stored 6.56168 ft]; Custom Window Height=1490 mm  [stored 4.88845 ft]; Custom Window Width=2390 mm  [stored 7.84121 ft]; Energy Advantage SHGC Value=0.638; Energy Advantage U Value=4.55; Heavy Duty Interlocker=Yes; Height=1490 mm  [stored 4.88845 ft]; Intruderprufe LowE SHGC Value=0.59; Intruderprufe LowE U Value=4.33; Intruderprufe SHGC Value=0.675; Intruderprufe U Value=5.95; Is Heavy Duty Mullion=1 mm  [stored 0.00328084 ft]; Limit Sash Width Left Max=1500 mm  [stored 4.92126 ft]; Limit Sash Width Left Min=891 mm; Max Pane Area=1.46 m²; Sash Height=1433 mm; Sash Width Left=1196 mm; Sash Width Right=1196 mm; Standard Interlocker=No; Width=2390 mm  [stored 7.84121 ft]; Windload Design=2000 mm  [stored 6.56168 ft]
- 1000SW-2418XO-1500Pa: Area Left Sash Glazing=1.79 m²; Area Right Sash Glazing=1.79 m²; Clearvue SHGC Value=0.728; Clearvue U Value=6.17; Custom Windload=1500 mm  [stored 4.92126 ft]; Custom Window Height=1790 mm  [stored 5.8727 ft]; Custom Window Width=2390 mm  [stored 7.84121 ft]; Energy Advantage SHGC Value=0.651; Energy Advantage U Value=4.45; Heavy Duty Interlocker=Yes; Height=1790 mm  [stored 5.8727 ft]; Intruderprufe LowE SHGC Value=0.425; Intruderprufe LowE U Value=4.28; Intruderprufe SHGC Value=0.689; Intruderprufe U Value=5.95; Is Heavy Duty Mullion=1 mm  [stored 0.00328084 ft]; Limit Sash Width Left Max=1500 mm  [stored 4.92126 ft]; Limit Sash Width Left Min=891 mm; Max Pane Area=1.79 m²; Sash Height=1733 mm; Sash Width Left=1196 mm; Sash Width Right=1196 mm; Standard Interlocker=No; Width=2390 mm  [stored 7.84121 ft]; Windload Design=1500 mm  [stored 4.92126 ft]
- 1000SW-2418XO-2000Pa: Area Left Sash Glazing=1.79 m²; Area Right Sash Glazing=1.79 m²; Clearvue SHGC Value=0.728; Clearvue U Value=6.17; Custom Windload=2000 mm  [stored 6.56168 ft]; Custom Window Height=1790 mm  [stored 5.8727 ft]; Custom Window Width=2390 mm  [stored 7.84121 ft]; Energy Advantage SHGC Value=0.651; Energy Advantage U Value=4.45; Heavy Duty Interlocker=Yes; Height=1790 mm  [stored 5.8727 ft]; Intruderprufe LowE SHGC Value=0.425; Intruderprufe LowE U Value=4.28; Intruderprufe SHGC Value=0.689; Intruderprufe U Value=5.95; Is Heavy Duty Mullion=1 mm  [stored 0.00328084 ft]; Limit Sash Width Left Max=1500 mm  [stored 4.92126 ft]; Limit Sash Width Left Min=891 mm; Max Pane Area=1.79 m²; Sash Height=1733 mm; Sash Width Left=1196 mm; Sash Width Right=1196 mm; Standard Interlocker=No; Width=2390 mm  [stored 7.84121 ft]; Windload Design=2000 mm  [stored 6.56168 ft]
- 1000SW-2706XO-1500Pa: Area Left Sash Glazing=0.54 m²; Area Right Sash Glazing=0.54 m²; Clearvue SHGC Value=0.588; Clearvue U Value=6.75; Custom Windload=1500 mm  [stored 4.92126 ft]; Custom Window Height=590 mm  [stored 1.9357 ft]; Custom Window Width=2690 mm; Energy Advantage SHGC Value=0.528; Energy Advantage U Value=5.44; Heavy Duty Interlocker=No; Height=590 mm  [stored 1.9357 ft]; Intruderprufe LowE SHGC Value=0.482; Intruderprufe LowE U Value=4.99; Intruderprufe SHGC Value=0.544; Intruderprufe U Value=6.25; Is Heavy Duty Mullion=0 mm  [stored 0 ft]; Limit Sash Width Left Max=1500 mm  [stored 4.92126 ft]; Limit Sash Width Left Min=1191 mm; Max Pane Area=0.54 m²; Sash Height=533 mm; Sash Width Left=1346 mm; Sash Width Right=1346 mm; Standard Interlocker=Yes; Width=2690 mm; Windload Design=1500 mm  [stored 4.92126 ft]
- 1000SW-2706XO-2000Pa: Area Left Sash Glazing=0.54 m²; Area Right Sash Glazing=0.54 m²; Clearvue SHGC Value=0.588; Clearvue U Value=6.75; Custom Windload=2000 mm  [stored 6.56168 ft]; Custom Window Height=590 mm  [stored 1.9357 ft]; Custom Window Width=2690 mm; Energy Advantage SHGC Value=0.528; Energy Advantage U Value=5.44; Heavy Duty Interlocker=No; Height=590 mm  [stored 1.9357 ft]; Intruderprufe LowE SHGC Value=0.482; Intruderprufe LowE U Value=4.99; Intruderprufe SHGC Value=0.544; Intruderprufe U Value=6.25; Is Heavy Duty Mullion=0 mm  [stored 0 ft]; Limit Sash Width Left Max=1500 mm  [stored 4.92126 ft]; Limit Sash Width Left Min=1191 mm; Max Pane Area=0.54 m²; Sash Height=533 mm; Sash Width Left=1346 mm; Sash Width Right=1346 mm; Standard Interlocker=Yes; Width=2690 mm; Windload Design=2000 mm  [stored 6.56168 ft]
- 1000SW-2709XO-1500Pa: Area Left Sash Glazing=0.91 m²; Area Right Sash Glazing=0.91 m²; Clearvue SHGC Value=0.661; Clearvue U Value=6.46; Custom Windload=1500 mm  [stored 4.92126 ft]; Custom Window Height=890 mm  [stored 2.91995 ft]; Custom Window Width=2690 mm; Energy Advantage SHGC Value=0.592; Energy Advantage U Value=4.93; Heavy Duty Interlocker=No; Height=890 mm  [stored 2.91995 ft]; Intruderprufe LowE SHGC Value=0.545; Intruderprufe LowE U Value=4.61; Intruderprufe SHGC Value=0.624; Intruderprufe U Value=6.08; Is Heavy Duty Mullion=0 mm  [stored 0 ft]; Limit Sash Width Left Max=1500 mm  [stored 4.92126 ft]; Limit Sash Width Left Min=1191 mm; Max Pane Area=0.91 m²; Sash Height=833 mm; Sash Width Left=1346 mm; Sash Width Right=1346 mm; Standard Interlocker=Yes; Width=2690 mm; Windload Design=1500 mm  [stored 4.92126 ft]
- 1000SW-2709XO-2000Pa: Area Left Sash Glazing=0.91 m²; Area Right Sash Glazing=0.91 m²; Clearvue SHGC Value=0.661; Clearvue U Value=6.46; Custom Windload=2000 mm  [stored 6.56168 ft]; Custom Window Height=890 mm  [stored 2.91995 ft]; Custom Window Width=2690 mm; Energy Advantage SHGC Value=0.592; Energy Advantage U Value=4.93; Heavy Duty Interlocker=No; Height=890 mm  [stored 2.91995 ft]; Intruderprufe LowE SHGC Value=0.545; Intruderprufe LowE U Value=4.61; Intruderprufe SHGC Value=0.624; Intruderprufe U Value=6.08; Is Heavy Duty Mullion=0 mm  [stored 0 ft]; Limit Sash Width Left Max=1500 mm  [stored 4.92126 ft]; Limit Sash Width Left Min=1191 mm; Max Pane Area=0.91 m²; Sash Height=833 mm; Sash Width Left=1346 mm; Sash Width Right=1346 mm; Standard Interlocker=Yes; Width=2690 mm; Windload Design=2000 mm  [stored 6.56168 ft]
- 1000SW-2712XO-1500Pa: Area Left Sash Glazing=1.28 m²; Area Right Sash Glazing=1.28 m²; Clearvue SHGC Value=0.679; Clearvue U Value=6.31; Custom Windload=1500 mm  [stored 4.92126 ft]; Custom Window Height=1190 mm  [stored 3.9042 ft]; Custom Window Width=2690 mm; Energy Advantage SHGC Value=0.624; Energy Advantage U Value=4.68; Heavy Duty Interlocker=No; Height=1190 mm  [stored 3.9042 ft]; Intruderprufe LowE SHGC Value=0.576; Intruderprufe LowE U Value=4.42; Intruderprufe SHGC Value=0.659; Intruderprufe U Value=6; Is Heavy Duty Mullion=0 mm  [stored 0 ft]; Limit Sash Width Left Max=1500 mm  [stored 4.92126 ft]; Limit Sash Width Left Min=1191 mm; Max Pane Area=1.28 m²; Sash Height=1133 mm; Sash Width Left=1346 mm; Sash Width Right=1346 mm; Standard Interlocker=Yes; Width=2690 mm; Windload Design=1500 mm  [stored 4.92126 ft]
- 1000SW-2712XO-2000Pa: Area Left Sash Glazing=1.28 m²; Area Right Sash Glazing=1.28 m²; Clearvue SHGC Value=0.679; Clearvue U Value=6.31; Custom Windload=2000 mm  [stored 6.56168 ft]; Custom Window Height=1190 mm  [stored 3.9042 ft]; Custom Window Width=2690 mm; Energy Advantage SHGC Value=0.624; Energy Advantage U Value=4.68; Heavy Duty Interlocker=No; Height=1190 mm  [stored 3.9042 ft]; Intruderprufe LowE SHGC Value=0.576; Intruderprufe LowE U Value=4.42; Intruderprufe SHGC Value=0.659; Intruderprufe U Value=6; Is Heavy Duty Mullion=0 mm  [stored 0 ft]; Limit Sash Width Left Max=1500 mm  [stored 4.92126 ft]; Limit Sash Width Left Min=1191 mm; Max Pane Area=1.28 m²; Sash Height=1133 mm; Sash Width Left=1346 mm; Sash Width Right=1346 mm; Standard Interlocker=Yes; Width=2690 mm; Windload Design=2000 mm  [stored 6.56168 ft]
- 1000SW-2715XO-1500Pa: Area Left Sash Glazing=1.66 m²; Area Right Sash Glazing=1.66 m²; Clearvue SHGC Value=0.719; Clearvue U Value=6.23; Custom Windload=1500 mm  [stored 4.92126 ft]; Custom Window Height=1490 mm  [stored 4.88845 ft]; Custom Window Width=2690 mm; Energy Advantage SHGC Value=0.643; Energy Advantage U Value=4.53; Heavy Duty Interlocker=Yes; Height=1490 mm  [stored 4.88845 ft]; Intruderprufe LowE SHGC Value=0.594; Intruderprufe LowE U Value=4.3; Intruderprufe SHGC Value=0.68; Intruderprufe U Value=5.95; Is Heavy Duty Mullion=1 mm  [stored 0.00328084 ft]; Limit Sash Width Left Max=1500 mm  [stored 4.92126 ft]; Limit Sash Width Left Min=1191 mm; Max Pane Area=1.66 m²; Sash Height=1433 mm; Sash Width Left=1346 mm; Sash Width Right=1346 mm; Standard Interlocker=No; Width=2690 mm; Windload Design=1500 mm  [stored 4.92126 ft]
- 1000SW-2715XO-2000Pa: Area Left Sash Glazing=1.66 m²; Area Right Sash Glazing=1.66 m²; Clearvue SHGC Value=0.719; Clearvue U Value=6.23; Custom Windload=2000 mm  [stored 6.56168 ft]; Custom Window Height=1490 mm  [stored 4.88845 ft]; Custom Window Width=2690 mm; Energy Advantage SHGC Value=0.643; Energy Advantage U Value=4.53; Heavy Duty Interlocker=Yes; Height=1490 mm  [stored 4.88845 ft]; Intruderprufe LowE SHGC Value=0.594; Intruderprufe LowE U Value=4.3; Intruderprufe SHGC Value=0.68; Intruderprufe U Value=5.95; Is Heavy Duty Mullion=1 mm  [stored 0.00328084 ft]; Limit Sash Width Left Max=1500 mm  [stored 4.92126 ft]; Limit Sash Width Left Min=1191 mm; Max Pane Area=1.66 m²; Sash Height=1433 mm; Sash Width Left=1346 mm; Sash Width Right=1346 mm; Standard Interlocker=No; Width=2690 mm; Windload Design=2000 mm  [stored 6.56168 ft]
- 1000SW-2718XO-1500Pa: Area Left Sash Glazing=2.03 m²; Area Right Sash Glazing=2.03 m²; Clearvue SHGC Value=0.733; Clearvue U Value=6.17; Custom Windload=1500 mm  [stored 4.92126 ft]; Custom Window Height=1790 mm  [stored 5.8727 ft]; Custom Window Width=2690 mm; Energy Advantage SHGC Value=0.655; Energy Advantage U Value=4.43; Heavy Duty Interlocker=Yes; Height=1790 mm  [stored 5.8727 ft]; Intruderprufe LowE SHGC Value=0.607; Intruderprufe LowE U Value=4.23; Intruderprufe SHGC Value=0.694; Intruderprufe U Value=5.92; Is Heavy Duty Mullion=1 mm  [stored 0.00328084 ft]; Limit Sash Width Left Max=1500 mm  [stored 4.92126 ft]; Limit Sash Width Left Min=1191 mm; Max Pane Area=2.03 m²; Sash Height=1733 mm; Sash Width Left=1346 mm; Sash Width Right=1346 mm; Standard Interlocker=No; Width=2690 mm; Windload Design=1500 mm  [stored 4.92126 ft]
- 1000SW-2718XO-2000Pa: Area Left Sash Glazing=2.03 m²; Area Right Sash Glazing=2.03 m²; Clearvue SHGC Value=0.733; Clearvue U Value=6.17; Custom Windload=2000 mm  [stored 6.56168 ft]; Custom Window Height=1790 mm  [stored 5.8727 ft]; Custom Window Width=2690 mm; Energy Advantage SHGC Value=0.655; Energy Advantage U Value=4.43; Heavy Duty Interlocker=Yes; Height=1790 mm  [stored 5.8727 ft]; Intruderprufe LowE SHGC Value=0.607; Intruderprufe LowE U Value=4.23; Intruderprufe SHGC Value=0.694; Intruderprufe U Value=5.92; Is Heavy Duty Mullion=1 mm  [stored 0.00328084 ft]; Limit Sash Width Left Max=1500 mm  [stored 4.92126 ft]; Limit Sash Width Left Min=1191 mm; Max Pane Area=2.03 m²; Sash Height=1733 mm; Sash Width Left=1346 mm; Sash Width Right=1346 mm; Standard Interlocker=No; Width=2690 mm; Windload Design=2000 mm  [stored 6.56168 ft]
- 1000SW-3006XO-1500Pa: Area Left Sash Glazing=0.6 m²; Area Right Sash Glazing=0.6 m²; Clearvue SHGC Value=0.592; Clearvue U Value=6.76; Custom Windload=1500 mm  [stored 4.92126 ft]; Custom Window Height=590 mm  [stored 1.9357 ft]; Custom Window Width=2990 mm  [stored 9.80971 ft]; Energy Advantage SHGC Value=0.531; Energy Advantage U Value=5.43; Heavy Duty Interlocker=No; Height=590 mm  [stored 1.9357 ft]; Intruderprufe LowE SHGC Value=0.484; Intruderprufe LowE U Value=4.98; Intruderprufe SHGC Value=0.557; Intruderprufe U Value=6.25; Is Heavy Duty Mullion=0 mm  [stored 0 ft]; Limit Sash Width Left Max=1500 mm  [stored 4.92126 ft]; Limit Sash Width Left Min=1491 mm; Max Pane Area=0.6 m²; Sash Height=533 mm; Sash Width Left=1496 mm; Sash Width Right=1496 mm; Standard Interlocker=Yes; Width=2990 mm  [stored 9.80971 ft]; Windload Design=1500 mm  [stored 4.92126 ft]
- 1000SW-3006XO-2000Pa: Area Left Sash Glazing=0.6 m²; Area Right Sash Glazing=0.6 m²; Clearvue SHGC Value=0.592; Clearvue U Value=6.76; Custom Windload=2000 mm  [stored 6.56168 ft]; Custom Window Height=590 mm  [stored 1.9357 ft]; Custom Window Width=2990 mm  [stored 9.80971 ft]; Energy Advantage SHGC Value=0.531; Energy Advantage U Value=5.43; Heavy Duty Interlocker=No; Height=590 mm  [stored 1.9357 ft]; Intruderprufe LowE SHGC Value=0.484; Intruderprufe LowE U Value=4.98; Intruderprufe SHGC Value=0.557; Intruderprufe U Value=6.25; Is Heavy Duty Mullion=0 mm  [stored 0 ft]; Limit Sash Width Left Max=1500 mm  [stored 4.92126 ft]; Limit Sash Width Left Min=1491 mm; Max Pane Area=0.6 m²; Sash Height=533 mm; Sash Width Left=1496 mm; Sash Width Right=1496 mm; Standard Interlocker=Yes; Width=2990 mm  [stored 9.80971 ft]; Windload Design=2000 mm  [stored 6.56168 ft]
- 1000SW-3009XO-1500Pa: Area Left Sash Glazing=1.02 m²; Area Right Sash Glazing=1.02 m²; Clearvue SHGC Value=0.665; Clearvue U Value=6.46; Custom Windload=1500 mm  [stored 4.92126 ft]; Custom Window Height=890 mm  [stored 2.91995 ft]; Custom Window Width=2990 mm  [stored 9.80971 ft]; Energy Advantage SHGC Value=0.595; Energy Advantage U Value=4.92; Heavy Duty Interlocker=No; Height=890 mm  [stored 2.91995 ft]; Intruderprufe LowE SHGC Value=0.548; Intruderprufe LowE U Value=4.59; Intruderprufe SHGC Value=0.628; Intruderprufe U Value=6.08; Is Heavy Duty Mullion=0 mm  [stored 0 ft]; Limit Sash Width Left Max=1500 mm  [stored 4.92126 ft]; Limit Sash Width Left Min=1491 mm; Max Pane Area=1.02 m²; Sash Height=833 mm; Sash Width Left=1496 mm; Sash Width Right=1496 mm; Standard Interlocker=Yes; Width=2990 mm  [stored 9.80971 ft]; Windload Design=1500 mm  [stored 4.92126 ft]
- 1000SW-3009XO-2000Pa: Area Left Sash Glazing=1.02 m²; Area Right Sash Glazing=1.02 m²; Clearvue SHGC Value=0.665; Clearvue U Value=6.46; Custom Windload=2000 mm  [stored 6.56168 ft]; Custom Window Height=890 mm  [stored 2.91995 ft]; Custom Window Width=2990 mm  [stored 9.80971 ft]; Energy Advantage SHGC Value=0.595; Energy Advantage U Value=4.92; Heavy Duty Interlocker=No; Height=890 mm  [stored 2.91995 ft]; Intruderprufe LowE SHGC Value=0.548; Intruderprufe LowE U Value=4.59; Intruderprufe SHGC Value=0.628; Intruderprufe U Value=6.08; Is Heavy Duty Mullion=0 mm  [stored 0 ft]; Limit Sash Width Left Max=1500 mm  [stored 4.92126 ft]; Limit Sash Width Left Min=1491 mm; Max Pane Area=1.02 m²; Sash Height=833 mm; Sash Width Left=1496 mm; Sash Width Right=1496 mm; Standard Interlocker=Yes; Width=2990 mm  [stored 9.80971 ft]; Windload Design=2000 mm  [stored 6.56168 ft]
- 1000SW-3012XO-1500Pa: Area Left Sash Glazing=1.44 m²; Area Right Sash Glazing=1.44 m²; Clearvue SHGC Value=0.701; Clearvue U Value=6.31; Custom Windload=1500 mm  [stored 4.92126 ft]; Custom Window Height=1190 mm  [stored 3.9042 ft]; Custom Window Width=2990 mm  [stored 9.80971 ft]; Energy Advantage SHGC Value=0.627; Energy Advantage U Value=4.66; Heavy Duty Interlocker=No; Height=1190 mm  [stored 3.9042 ft]; Intruderprufe LowE SHGC Value=0.579; Intruderprufe LowE U Value=4.4; Intruderprufe SHGC Value=0.663; Intruderprufe U Value=6; Is Heavy Duty Mullion=0 mm  [stored 0 ft]; Limit Sash Width Left Max=1500 mm  [stored 4.92126 ft]; Limit Sash Width Left Min=1491 mm; Max Pane Area=1.44 m²; Sash Height=1133 mm; Sash Width Left=1496 mm; Sash Width Right=1496 mm; Standard Interlocker=Yes; Width=2990 mm  [stored 9.80971 ft]; Windload Design=1500 mm  [stored 4.92126 ft]
- 1000SW-3012XO-2000Pa: Area Left Sash Glazing=1.44 m²; Area Right Sash Glazing=1.44 m²; Clearvue SHGC Value=0.701; Clearvue U Value=6.31; Custom Windload=2000 mm  [stored 6.56168 ft]; Custom Window Height=1190 mm  [stored 3.9042 ft]; Custom Window Width=2990 mm  [stored 9.80971 ft]; Energy Advantage SHGC Value=0.627; Energy Advantage U Value=4.66; Heavy Duty Interlocker=No; Height=1190 mm  [stored 3.9042 ft]; Intruderprufe LowE SHGC Value=0.579; Intruderprufe LowE U Value=4.4; Intruderprufe SHGC Value=0.663; Intruderprufe U Value=6; Is Heavy Duty Mullion=0 mm  [stored 0 ft]; Limit Sash Width Left Max=1500 mm  [stored 4.92126 ft]; Limit Sash Width Left Min=1491 mm; Max Pane Area=1.44 m²; Sash Height=1133 mm; Sash Width Left=1496 mm; Sash Width Right=1496 mm; Standard Interlocker=Yes; Width=2990 mm  [stored 9.80971 ft]; Windload Design=2000 mm  [stored 6.56168 ft]
- 1000SW-3015XO-1500Pa: Area Left Sash Glazing=1.86 m²; Area Right Sash Glazing=1.86 m²; Clearvue SHGC Value=0.723; Clearvue U Value=6.23; Custom Windload=1500 mm  [stored 4.92126 ft]; Custom Window Height=1490 mm  [stored 4.88845 ft]; Custom Window Width=2990 mm  [stored 9.80971 ft]; Energy Advantage SHGC Value=0.646; Energy Advantage U Value=4.51; Heavy Duty Interlocker=Yes; Height=1490 mm  [stored 4.88845 ft]; Intruderprufe LowE SHGC Value=0.598; Intruderprufe LowE U Value=4.28; Intruderprufe SHGC Value=0.684; Intruderprufe U Value=5.95; Is Heavy Duty Mullion=1 mm  [stored 0.00328084 ft]; Limit Sash Width Left Max=1500 mm  [stored 4.92126 ft]; Limit Sash Width Left Min=1491 mm; Max Pane Area=1.86 m²; Sash Height=1433 mm; Sash Width Left=1496 mm; Sash Width Right=1496 mm; Standard Interlocker=No; Width=2990 mm  [stored 9.80971 ft]; Windload Design=1500 mm  [stored 4.92126 ft]
- 1000SW-3015XO-2000Pa: Area Left Sash Glazing=1.86 m²; Area Right Sash Glazing=1.86 m²; Clearvue SHGC Value=0.723; Clearvue U Value=6.23; Custom Windload=2000 mm  [stored 6.56168 ft]; Custom Window Height=1490 mm  [stored 4.88845 ft]; Custom Window Width=2990 mm  [stored 9.80971 ft]; Energy Advantage SHGC Value=0.646; Energy Advantage U Value=4.51; Heavy Duty Interlocker=Yes; Height=1490 mm  [stored 4.88845 ft]; Intruderprufe LowE SHGC Value=0.598; Intruderprufe LowE U Value=4.28; Intruderprufe SHGC Value=0.684; Intruderprufe U Value=5.95; Is Heavy Duty Mullion=1 mm  [stored 0.00328084 ft]; Limit Sash Width Left Max=1500 mm  [stored 4.92126 ft]; Limit Sash Width Left Min=1491 mm; Max Pane Area=1.86 m²; Sash Height=1433 mm; Sash Width Left=1496 mm; Sash Width Right=1496 mm; Standard Interlocker=No; Width=2990 mm  [stored 9.80971 ft]; Windload Design=2000 mm  [stored 6.56168 ft]
- 1000SW-3018XO-1500Pa: Area Left Sash Glazing=2.28 m²; Area Right Sash Glazing=2.28 m²; Clearvue SHGC Value=0.737; Clearvue U Value=6.17; Custom Windload=1500 mm  [stored 4.92126 ft]; Custom Window Height=1790 mm  [stored 5.8727 ft]; Custom Window Width=2990 mm  [stored 9.80971 ft]; Energy Advantage SHGC Value=0.659; Energy Advantage U Value=4.41; Heavy Duty Interlocker=Yes; Height=1790 mm  [stored 5.8727 ft]; Intruderprufe LowE SHGC Value=0.61; Intruderprufe LowE U Value=4.21; Intruderprufe SHGC Value=0.698; Intruderprufe U Value=5.92; Is Heavy Duty Mullion=1 mm  [stored 0.00328084 ft]; Limit Sash Width Left Max=1500 mm  [stored 4.92126 ft]; Limit Sash Width Left Min=1491 mm; Max Pane Area=2.28 m²; Sash Height=1733 mm; Sash Width Left=1496 mm; Sash Width Right=1496 mm; Standard Interlocker=No; Width=2990 mm  [stored 9.80971 ft]; Windload Design=1500 mm  [stored 4.92126 ft]
- 1000SW-3018XO-2000Pa: Area Left Sash Glazing=2.28 m²; Area Right Sash Glazing=2.28 m²; Clearvue SHGC Value=0.737; Clearvue U Value=6.17; Custom Windload=2000 mm  [stored 6.56168 ft]; Custom Window Height=1790 mm  [stored 5.8727 ft]; Custom Window Width=2990 mm  [stored 9.80971 ft]; Energy Advantage SHGC Value=0.659; Energy Advantage U Value=4.41; Heavy Duty Interlocker=Yes; Height=1790 mm  [stored 5.8727 ft]; Intruderprufe LowE SHGC Value=0.61; Intruderprufe LowE U Value=4.21; Intruderprufe SHGC Value=0.698; Intruderprufe U Value=5.92; Is Heavy Duty Mullion=1 mm  [stored 0.00328084 ft]; Limit Sash Width Left Max=1500 mm  [stored 4.92126 ft]; Limit Sash Width Left Min=1491 mm; Max Pane Area=2.28 m²; Sash Height=1733 mm; Sash Width Left=1496 mm; Sash Width Right=1496 mm; Standard Interlocker=No; Width=2990 mm  [stored 9.80971 ft]; Windload Design=2000 mm  [stored 6.56168 ft]

note: [stored X ft] marks values corroborated as IEEE doubles in the binary element streams (Revit-internal decimal feet)

## geometry (parser evidence)
native form markers: Sweep x11
no freeform markers — native parametric forms only
